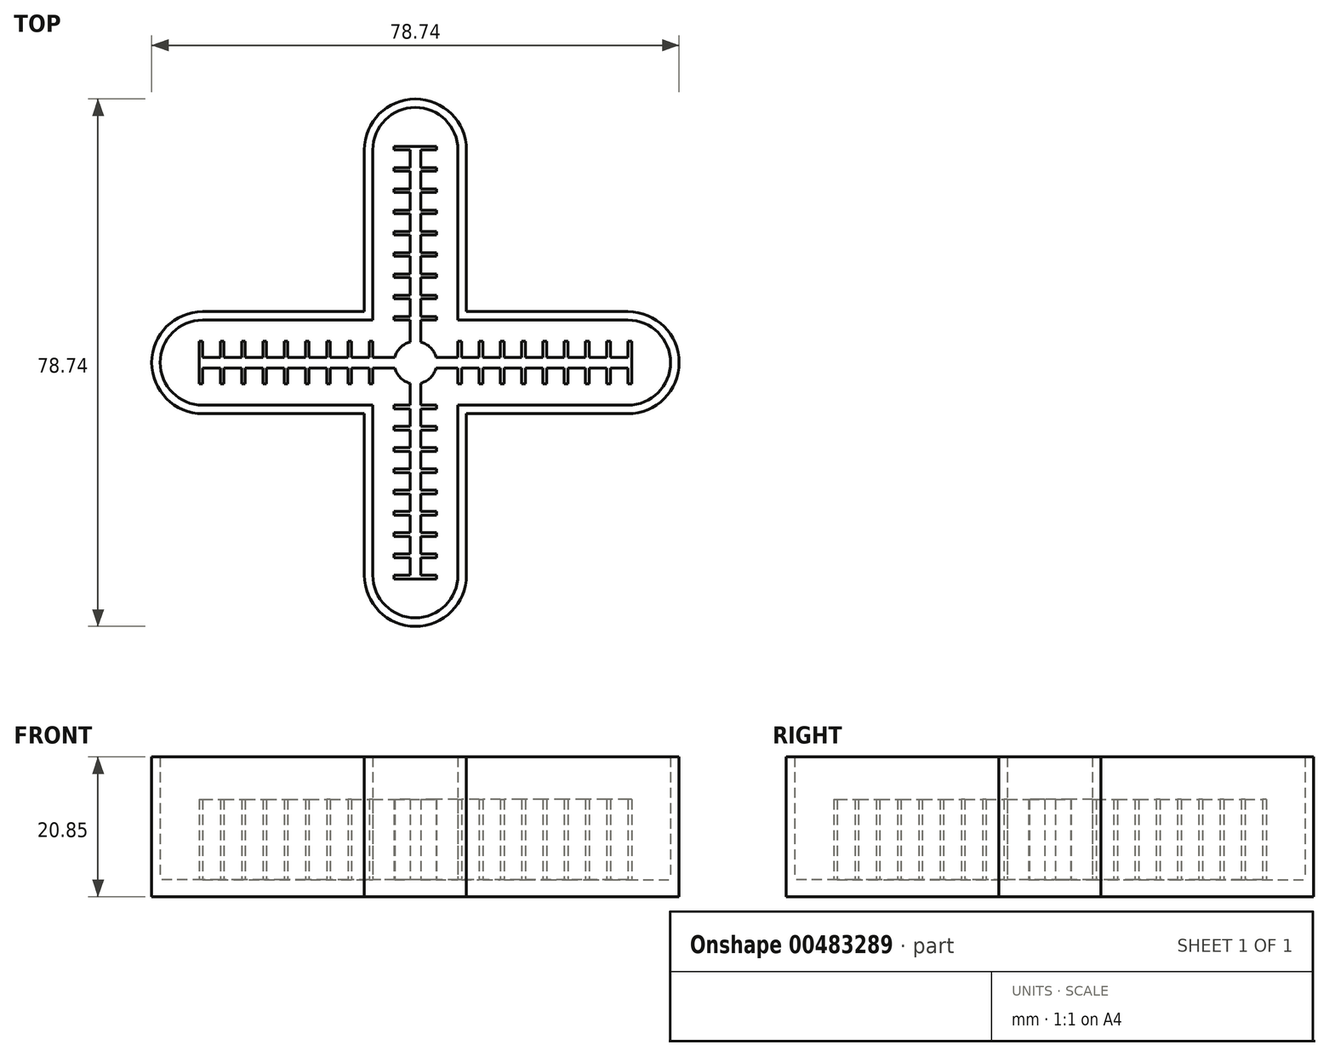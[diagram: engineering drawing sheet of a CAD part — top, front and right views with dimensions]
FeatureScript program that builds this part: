
annotation { "Feature Type Name" : "Feature", "Feature Type Description" : "" }
export const myFeature = defineFeature(function(context is Context, id is Id, definition is map)
    precondition{}
    {
        {
            var Q0;
            Q0=qCreatedBy(makeId("Top.planeOp"),FACE);
            var sketch = newSketch(context, id + "F0", { "sketchPlane" : qUnion([Q0])});
            skLineSegment(sketch, "E0", {"start": v(0, 0) * mm, "end": v(0, 25.4) * mm});
            skArc(sketch, "E1", {"start": v(6.35, 25.4) * mm, "mid": v(0, 31.75) * mm, "end": v(-6.35, 25.4) * mm});
            skLineSegment(sketch, "E2", {"start": v(6.35, 25.4) * mm, "end": v(6.35, 0) * mm});
            skLineSegment(sketch, "E3", {"start": v(-6.35, 25.4) * mm, "end": v(-6.35, 0) * mm});
            skLineSegment(sketch, "E4", {"start": v(6.35, 0) * mm, "end": v(31.75, 0) * mm});
            skLineSegment(sketch, "E5.0", {"start": v(6.35, -12.7) * mm, "end": v(31.75, -12.7) * mm});
            skArc(sketch, "E6", {"start": v(31.75, -12.7) * mm, "mid": v(38.1, -6.35) * mm, "end": v(31.75, 0) * mm});
            skLineSegment(sketch, "E7", {"start": v(31.75, -6.35) * mm, "end": v(6.35, -6.35) * mm});
            skLineSegment(sketch, "E8", {"start": v(6.35, -12.7) * mm, "end": v(6.35, -38.1) * mm});
            skLineSegment(sketch, "E9.0", {"start": v(-6.35, -12.7) * mm, "end": v(-6.35, -38.1) * mm});
            skArc(sketch, "E10", {"start": v(-6.35, -38.1) * mm, "mid": v(0, -44.45) * mm, "end": v(6.35, -38.1) * mm});
            skLineSegment(sketch, "E11", {"start": v(0, -38.1) * mm, "end": v(0, -12.7) * mm});
            skLineSegment(sketch, "E12", {"start": v(-6.35, -12.7) * mm, "end": v(-31.75, -12.7) * mm});
            skLineSegment(sketch, "E13.0", {"start": v(-6.35, 0) * mm, "end": v(-31.75, 0) * mm});
            skArc(sketch, "E14", {"start": v(-31.75, 0) * mm, "mid": v(-38.1, -6.35) * mm, "end": v(-31.75, -12.7) * mm});
            skLineSegment(sketch, "E15", {"start": v(-31.75, -6.35) * mm, "end": v(-6.35, -6.35) * mm});
            skLineSegment(sketch, "E16", {"start": v(-3.17, 0) * mm, "end": v(3.18, 0) * mm});
            skLineSegment(sketch, "E17.0", {"start": v(-3.17, 3.18) * mm, "end": v(3.18, 3.18) * mm});
            skLineSegment(sketch, "E18.0", {"start": v(-3.17, 6.35) * mm, "end": v(3.18, 6.35) * mm});
            skLineSegment(sketch, "E19.0", {"start": v(-3.17, 9.53) * mm, "end": v(3.18, 9.53) * mm});
            skLineSegment(sketch, "E20.0", {"start": v(-3.17, 12.7) * mm, "end": v(3.18, 12.7) * mm});
            skLineSegment(sketch, "E21.0", {"start": v(-3.17, 15.88) * mm, "end": v(3.18, 15.88) * mm});
            skLineSegment(sketch, "E22.0", {"start": v(-3.17, 19.05) * mm, "end": v(3.18, 19.05) * mm});
            skLineSegment(sketch, "E23.0", {"start": v(-3.17, 22.23) * mm, "end": v(3.18, 22.23) * mm});
            skLineSegment(sketch, "E24.0", {"start": v(-3.17, 25.4) * mm, "end": v(3.18, 25.4) * mm});
            skLineSegment(sketch, "E25.1.0", {"start": v(-31.75, -9.52) * mm, "end": v(-31.75, -3.17) * mm});
            skLineSegment(sketch, "E25.1.1", {"start": v(-28.58, -9.52) * mm, "end": v(-28.58, -3.17) * mm});
            skLineSegment(sketch, "E25.1.2", {"start": v(-25.4, -9.52) * mm, "end": v(-25.4, -3.17) * mm});
            skLineSegment(sketch, "E25.1.3", {"start": v(-22.23, -9.52) * mm, "end": v(-22.23, -3.17) * mm});
            skLineSegment(sketch, "E25.1.4", {"start": v(-19.05, -9.52) * mm, "end": v(-19.05, -3.17) * mm});
            skLineSegment(sketch, "E25.1.5", {"start": v(-15.88, -9.52) * mm, "end": v(-15.88, -3.17) * mm});
            skLineSegment(sketch, "E25.1.6", {"start": v(-12.7, -9.52) * mm, "end": v(-12.7, -3.17) * mm});
            skLineSegment(sketch, "E25.1.7", {"start": v(-9.53, -9.52) * mm, "end": v(-9.53, -3.17) * mm});
            skLineSegment(sketch, "E25.1.8", {"start": v(-6.35, -9.52) * mm, "end": v(-6.35, -3.17) * mm});
            skLineSegment(sketch, "E25.2.0", {"start": v(3.17, -38.1) * mm, "end": v(-3.18, -38.1) * mm});
            skLineSegment(sketch, "E25.2.1", {"start": v(3.17, -34.92) * mm, "end": v(-3.18, -34.92) * mm});
            skLineSegment(sketch, "E25.2.2", {"start": v(3.17, -31.75) * mm, "end": v(-3.18, -31.75) * mm});
            skLineSegment(sketch, "E25.2.3", {"start": v(3.17, -28.57) * mm, "end": v(-3.18, -28.57) * mm});
            skLineSegment(sketch, "E25.2.4", {"start": v(3.17, -25.4) * mm, "end": v(-3.18, -25.4) * mm});
            skLineSegment(sketch, "E25.2.5", {"start": v(3.17, -22.23) * mm, "end": v(-3.18, -22.23) * mm});
            skLineSegment(sketch, "E25.2.6", {"start": v(3.17, -19.05) * mm, "end": v(-3.18, -19.05) * mm});
            skLineSegment(sketch, "E25.2.7", {"start": v(3.17, -15.88) * mm, "end": v(-3.18, -15.88) * mm});
            skLineSegment(sketch, "E25.2.8", {"start": v(3.17, -12.7) * mm, "end": v(-3.18, -12.7) * mm});
            skLineSegment(sketch, "E25.3.0", {"start": v(31.75, -3.18) * mm, "end": v(31.75, -9.53) * mm});
            skLineSegment(sketch, "E25.3.1", {"start": v(28.58, -3.18) * mm, "end": v(28.58, -9.53) * mm});
            skLineSegment(sketch, "E25.3.2", {"start": v(25.4, -3.18) * mm, "end": v(25.4, -9.53) * mm});
            skLineSegment(sketch, "E25.3.3", {"start": v(22.23, -3.18) * mm, "end": v(22.23, -9.53) * mm});
            skLineSegment(sketch, "E25.3.4", {"start": v(19.05, -3.18) * mm, "end": v(19.05, -9.53) * mm});
            skLineSegment(sketch, "E25.3.5", {"start": v(15.88, -3.18) * mm, "end": v(15.88, -9.53) * mm});
            skLineSegment(sketch, "E25.3.6", {"start": v(12.7, -3.18) * mm, "end": v(12.7, -9.53) * mm});
            skLineSegment(sketch, "E25.3.7", {"start": v(9.53, -3.18) * mm, "end": v(9.53, -9.53) * mm});
            skLineSegment(sketch, "E25.3.8", {"start": v(6.35, -3.18) * mm, "end": v(6.35, -9.53) * mm});
            skPoint(sketch, "E25.center", {"position": v(0, -6.35) * mm});
            skCircle(sketch, "E26", {"center": v(0, -6.35) * mm, "radius": 3.18 * mm});
            skLineSegment(sketch, "E27", {"start": v(6.35, -6.35) * mm, "end": v(3.18, -6.35) * mm});
            skLineSegment(sketch, "E28", {"start": v(0, 0) * mm, "end": v(0, -3.17) * mm});
            skLineSegment(sketch, "E29", {"start": v(-6.35, -6.35) * mm, "end": v(-3.18, -6.35) * mm});
            skLineSegment(sketch, "E30", {"start": v(0, -12.7) * mm, "end": v(0, -9.53) * mm});
            skLineSegment(sketch, "E31.0", {"start": v(0.8, -38.1) * mm, "end": v(0.8, -12.7) * mm});
            skLineSegment(sketch, "E32.0", {"start": v(-0.8, -38.1) * mm, "end": v(-0.8, -12.7) * mm});
            skLineSegment(sketch, "E33", {"start": v(-0.8, -12.7) * mm, "end": v(-0.8, -9.42) * mm});
            skLineSegment(sketch, "E34", {"start": v(0.8, -12.7) * mm, "end": v(0.8, -9.42) * mm});
            skLineSegment(sketch, "E35.0", {"start": v(31.75, -5.56) * mm, "end": v(6.35, -5.56) * mm});
            skLineSegment(sketch, "E36.0", {"start": v(31.75, -7.14) * mm, "end": v(6.35, -7.14) * mm});
            skLineSegment(sketch, "E37", {"start": v(6.35, -7.14) * mm, "end": v(3.07, -7.14) * mm});
            skLineSegment(sketch, "E38", {"start": v(6.35, -5.56) * mm, "end": v(3.07, -5.56) * mm});
            skLineSegment(sketch, "E39.0", {"start": v(0.8, 0) * mm, "end": v(0.8, 25.4) * mm});
            skLineSegment(sketch, "E40.0", {"start": v(-0.8, 0) * mm, "end": v(-0.8, 25.4) * mm});
            skLineSegment(sketch, "E41", {"start": v(-0.8, 0) * mm, "end": v(-0.8, -3.28) * mm});
            skLineSegment(sketch, "E42", {"start": v(0.8, 0) * mm, "end": v(0.8, -3.28) * mm});
            skLineSegment(sketch, "E43.0", {"start": v(-31.75, -7.14) * mm, "end": v(-6.35, -7.14) * mm});
            skLineSegment(sketch, "E44.0", {"start": v(-31.75, -5.56) * mm, "end": v(-6.35, -5.56) * mm});
            skLineSegment(sketch, "E45", {"start": v(-6.35, -5.56) * mm, "end": v(-3.07, -5.56) * mm});
            skLineSegment(sketch, "E46", {"start": v(-6.35, -7.14) * mm, "end": v(-3.07, -7.14) * mm});
            skLineSegment(sketch, "E47.0", {"start": v(7.62, 25.4) * mm, "end": v(7.62, 1.27) * mm});
            skLineSegment(sketch, "E47.1", {"start": v(-7.62, -13.97) * mm, "end": v(-31.75, -13.97) * mm});
            skArc(sketch, "E47.2", {"start": v(-31.75, 1.27) * mm, "mid": v(-39.37, -6.35) * mm, "end": v(-31.75, -13.97) * mm});
            skLineSegment(sketch, "E47.3", {"start": v(-7.62, 1.27) * mm, "end": v(-31.75, 1.27) * mm});
            skLineSegment(sketch, "E47.4", {"start": v(-7.62, 25.4) * mm, "end": v(-7.62, 1.27) * mm});
            skLineSegment(sketch, "E47.5", {"start": v(-7.62, -13.97) * mm, "end": v(-7.62, -38.1) * mm});
            skArc(sketch, "E47.6", {"start": v(7.62, 25.4) * mm, "mid": v(0, 33.02) * mm, "end": v(-7.62, 25.4) * mm});
            skArc(sketch, "E47.7", {"start": v(-7.62, -38.1) * mm, "mid": v(0, -45.72) * mm, "end": v(7.62, -38.1) * mm});
            skLineSegment(sketch, "E47.8", {"start": v(7.62, -13.97) * mm, "end": v(7.62, -38.1) * mm});
            skLineSegment(sketch, "E47.9", {"start": v(7.62, -13.97) * mm, "end": v(31.75, -13.97) * mm});
            skArc(sketch, "E47.10", {"start": v(31.75, -13.97) * mm, "mid": v(39.37, -6.35) * mm, "end": v(31.75, 1.27) * mm});
            skLineSegment(sketch, "E47.11", {"start": v(7.62, 1.27) * mm, "end": v(31.75, 1.27) * mm});
            skLineSegment(sketch, "E48.0", {"start": v(6.88, -3.18) * mm, "end": v(6.88, -9.53) * mm});
            skLineSegment(sketch, "E49", {"start": v(6.35, -3.18) * mm, "end": v(6.88, -3.18) * mm});
            skLineSegment(sketch, "E50", {"start": v(6.35, -9.53) * mm, "end": v(6.88, -9.53) * mm});
            skLineSegment(sketch, "E51.0", {"start": v(10.05, -3.18) * mm, "end": v(10.05, -9.53) * mm});
            skLineSegment(sketch, "E52", {"start": v(9.53, -3.18) * mm, "end": v(10.05, -3.18) * mm});
            skLineSegment(sketch, "E53", {"start": v(9.53, -9.53) * mm, "end": v(10.05, -9.53) * mm});
            skLineSegment(sketch, "E54.0", {"start": v(13.23, -3.18) * mm, "end": v(13.23, -9.53) * mm});
            skLineSegment(sketch, "E55", {"start": v(12.7, -3.18) * mm, "end": v(13.23, -3.18) * mm});
            skLineSegment(sketch, "E56", {"start": v(12.7, -9.53) * mm, "end": v(13.23, -9.53) * mm});
            skLineSegment(sketch, "E57.0", {"start": v(16.4, -3.18) * mm, "end": v(16.4, -9.53) * mm});
            skLineSegment(sketch, "E58", {"start": v(16.4, -3.18) * mm, "end": v(15.88, -3.18) * mm});
            skLineSegment(sketch, "E59", {"start": v(16.4, -9.53) * mm, "end": v(15.88, -9.53) * mm});
            skLineSegment(sketch, "E60.0", {"start": v(19.58, -3.18) * mm, "end": v(19.58, -9.53) * mm});
            skLineSegment(sketch, "E61", {"start": v(19.58, -3.18) * mm, "end": v(19.05, -3.18) * mm});
            skLineSegment(sketch, "E62", {"start": v(19.58, -9.53) * mm, "end": v(19.05, -9.53) * mm});
            skLineSegment(sketch, "E63.0", {"start": v(22.75, -3.18) * mm, "end": v(22.75, -9.53) * mm});
            skLineSegment(sketch, "E64", {"start": v(22.75, -3.18) * mm, "end": v(22.23, -3.18) * mm});
            skLineSegment(sketch, "E65", {"start": v(22.75, -9.53) * mm, "end": v(22.23, -9.53) * mm});
            skLineSegment(sketch, "E66.0", {"start": v(25.93, -3.18) * mm, "end": v(25.93, -9.53) * mm});
            skLineSegment(sketch, "E67", {"start": v(25.93, -3.18) * mm, "end": v(25.4, -3.18) * mm});
            skLineSegment(sketch, "E68", {"start": v(25.93, -9.53) * mm, "end": v(25.4, -9.53) * mm});
            skLineSegment(sketch, "E69.0", {"start": v(29.1, -3.18) * mm, "end": v(29.1, -9.53) * mm});
            skLineSegment(sketch, "E70", {"start": v(29.1, -3.18) * mm, "end": v(28.58, -3.18) * mm});
            skLineSegment(sketch, "E71", {"start": v(29.1, -9.53) * mm, "end": v(28.58, -9.53) * mm});
            skLineSegment(sketch, "E72.0", {"start": v(32.28, -3.18) * mm, "end": v(32.28, -9.53) * mm});
            skLineSegment(sketch, "E73", {"start": v(32.28, -3.18) * mm, "end": v(31.75, -3.18) * mm});
            skLineSegment(sketch, "E74", {"start": v(32.28, -9.53) * mm, "end": v(31.75, -9.53) * mm});
            skLineSegment(sketch, "E75.1.0", {"start": v(-3.17, 25.93) * mm, "end": v(3.18, 25.93) * mm});
            skLineSegment(sketch, "E75.1.1", {"start": v(-3.17, 25.93) * mm, "end": v(-3.17, 25.4) * mm});
            skLineSegment(sketch, "E75.1.2", {"start": v(3.18, 25.93) * mm, "end": v(3.18, 25.4) * mm});
            skLineSegment(sketch, "E75.1.3", {"start": v(-3.17, 22.75) * mm, "end": v(3.18, 22.75) * mm});
            skLineSegment(sketch, "E75.1.4", {"start": v(3.18, 22.75) * mm, "end": v(3.18, 22.23) * mm});
            skLineSegment(sketch, "E75.1.5", {"start": v(-3.17, 22.75) * mm, "end": v(-3.17, 22.23) * mm});
            skLineSegment(sketch, "E75.1.6", {"start": v(-3.17, 19.58) * mm, "end": v(3.18, 19.58) * mm});
            skLineSegment(sketch, "E75.1.7", {"start": v(-3.17, 19.58) * mm, "end": v(-3.17, 19.05) * mm});
            skLineSegment(sketch, "E75.1.8", {"start": v(3.18, 19.58) * mm, "end": v(3.18, 19.05) * mm});
            skLineSegment(sketch, "E75.1.9", {"start": v(-3.17, 16.4) * mm, "end": v(3.18, 16.4) * mm});
            skLineSegment(sketch, "E75.1.10", {"start": v(-3.17, 16.4) * mm, "end": v(-3.17, 15.88) * mm});
            skLineSegment(sketch, "E75.1.11", {"start": v(3.18, 16.4) * mm, "end": v(3.18, 15.88) * mm});
            skLineSegment(sketch, "E75.1.12", {"start": v(-3.17, 13.23) * mm, "end": v(3.18, 13.23) * mm});
            skLineSegment(sketch, "E75.1.13", {"start": v(3.18, 13.23) * mm, "end": v(3.18, 12.7) * mm});
            skLineSegment(sketch, "E75.1.14", {"start": v(-3.17, 13.23) * mm, "end": v(-3.17, 12.7) * mm});
            skLineSegment(sketch, "E75.1.15", {"start": v(-3.17, 10.05) * mm, "end": v(3.18, 10.05) * mm});
            skLineSegment(sketch, "E75.1.16", {"start": v(-3.17, 10.05) * mm, "end": v(-3.17, 9.53) * mm});
            skLineSegment(sketch, "E75.1.17", {"start": v(3.18, 10.05) * mm, "end": v(3.18, 9.53) * mm});
            skLineSegment(sketch, "E75.1.18", {"start": v(-3.17, 6.88) * mm, "end": v(3.18, 6.88) * mm});
            skLineSegment(sketch, "E75.1.19", {"start": v(3.18, 6.35) * mm, "end": v(3.18, 6.88) * mm});
            skLineSegment(sketch, "E75.1.20", {"start": v(-3.17, 6.35) * mm, "end": v(-3.17, 6.88) * mm});
            skLineSegment(sketch, "E75.1.21", {"start": v(-3.17, 3.7) * mm, "end": v(3.18, 3.7) * mm});
            skLineSegment(sketch, "E75.1.22", {"start": v(3.18, 3.18) * mm, "end": v(3.18, 3.7) * mm});
            skLineSegment(sketch, "E75.1.23", {"start": v(-3.17, 3.18) * mm, "end": v(-3.17, 3.7) * mm});
            skLineSegment(sketch, "E75.1.24", {"start": v(3.18, 0) * mm, "end": v(3.18, 0.53) * mm});
            skLineSegment(sketch, "E75.1.25", {"start": v(-3.17, 0.53) * mm, "end": v(3.18, 0.53) * mm});
            skLineSegment(sketch, "E75.1.26", {"start": v(-3.17, 0) * mm, "end": v(-3.17, 0.53) * mm});
            skLineSegment(sketch, "E75.2.0", {"start": v(-32.28, -9.52) * mm, "end": v(-32.28, -3.17) * mm});
            skLineSegment(sketch, "E75.2.1", {"start": v(-32.28, -9.52) * mm, "end": v(-31.75, -9.52) * mm});
            skLineSegment(sketch, "E75.2.2", {"start": v(-32.28, -3.17) * mm, "end": v(-31.75, -3.17) * mm});
            skLineSegment(sketch, "E75.2.3", {"start": v(-29.1, -9.52) * mm, "end": v(-29.1, -3.17) * mm});
            skLineSegment(sketch, "E75.2.4", {"start": v(-29.1, -3.17) * mm, "end": v(-28.58, -3.17) * mm});
            skLineSegment(sketch, "E75.2.5", {"start": v(-29.1, -9.52) * mm, "end": v(-28.58, -9.52) * mm});
            skLineSegment(sketch, "E75.2.6", {"start": v(-25.93, -9.52) * mm, "end": v(-25.93, -3.17) * mm});
            skLineSegment(sketch, "E75.2.7", {"start": v(-25.93, -9.52) * mm, "end": v(-25.4, -9.52) * mm});
            skLineSegment(sketch, "E75.2.8", {"start": v(-25.93, -3.17) * mm, "end": v(-25.4, -3.17) * mm});
            skLineSegment(sketch, "E75.2.9", {"start": v(-22.75, -9.52) * mm, "end": v(-22.75, -3.17) * mm});
            skLineSegment(sketch, "E75.2.10", {"start": v(-22.75, -9.52) * mm, "end": v(-22.23, -9.52) * mm});
            skLineSegment(sketch, "E75.2.11", {"start": v(-22.75, -3.17) * mm, "end": v(-22.23, -3.17) * mm});
            skLineSegment(sketch, "E75.2.12", {"start": v(-19.58, -9.52) * mm, "end": v(-19.58, -3.17) * mm});
            skLineSegment(sketch, "E75.2.13", {"start": v(-19.58, -3.17) * mm, "end": v(-19.05, -3.17) * mm});
            skLineSegment(sketch, "E75.2.14", {"start": v(-19.58, -9.52) * mm, "end": v(-19.05, -9.52) * mm});
            skLineSegment(sketch, "E75.2.15", {"start": v(-16.4, -9.52) * mm, "end": v(-16.4, -3.17) * mm});
            skLineSegment(sketch, "E75.2.16", {"start": v(-16.4, -9.52) * mm, "end": v(-15.88, -9.52) * mm});
            skLineSegment(sketch, "E75.2.17", {"start": v(-16.4, -3.17) * mm, "end": v(-15.88, -3.17) * mm});
            skLineSegment(sketch, "E75.2.18", {"start": v(-13.23, -9.52) * mm, "end": v(-13.23, -3.17) * mm});
            skLineSegment(sketch, "E75.2.19", {"start": v(-12.7, -3.17) * mm, "end": v(-13.23, -3.17) * mm});
            skLineSegment(sketch, "E75.2.20", {"start": v(-12.7, -9.52) * mm, "end": v(-13.23, -9.52) * mm});
            skLineSegment(sketch, "E75.2.21", {"start": v(-10.05, -9.52) * mm, "end": v(-10.05, -3.17) * mm});
            skLineSegment(sketch, "E75.2.22", {"start": v(-9.52, -3.17) * mm, "end": v(-10.05, -3.17) * mm});
            skLineSegment(sketch, "E75.2.23", {"start": v(-9.53, -9.52) * mm, "end": v(-10.05, -9.52) * mm});
            skLineSegment(sketch, "E75.2.24", {"start": v(-6.35, -3.17) * mm, "end": v(-6.88, -3.17) * mm});
            skLineSegment(sketch, "E75.2.25", {"start": v(-6.88, -9.52) * mm, "end": v(-6.88, -3.17) * mm});
            skLineSegment(sketch, "E75.2.26", {"start": v(-6.35, -9.52) * mm, "end": v(-6.88, -9.52) * mm});
            skLineSegment(sketch, "E75.3.0", {"start": v(3.17, -38.63) * mm, "end": v(-3.18, -38.63) * mm});
            skLineSegment(sketch, "E75.3.1", {"start": v(3.17, -38.63) * mm, "end": v(3.17, -38.1) * mm});
            skLineSegment(sketch, "E75.3.2", {"start": v(-3.18, -38.63) * mm, "end": v(-3.18, -38.1) * mm});
            skLineSegment(sketch, "E75.3.3", {"start": v(3.17, -35.45) * mm, "end": v(-3.18, -35.45) * mm});
            skLineSegment(sketch, "E75.3.4", {"start": v(-3.18, -35.45) * mm, "end": v(-3.18, -34.92) * mm});
            skLineSegment(sketch, "E75.3.5", {"start": v(3.17, -35.45) * mm, "end": v(3.17, -34.93) * mm});
            skLineSegment(sketch, "E75.3.6", {"start": v(3.17, -32.28) * mm, "end": v(-3.18, -32.28) * mm});
            skLineSegment(sketch, "E75.3.7", {"start": v(3.17, -32.28) * mm, "end": v(3.17, -31.75) * mm});
            skLineSegment(sketch, "E75.3.8", {"start": v(-3.18, -32.28) * mm, "end": v(-3.18, -31.75) * mm});
            skLineSegment(sketch, "E75.3.9", {"start": v(3.17, -29.1) * mm, "end": v(-3.18, -29.1) * mm});
            skLineSegment(sketch, "E75.3.10", {"start": v(3.17, -29.1) * mm, "end": v(3.17, -28.58) * mm});
            skLineSegment(sketch, "E75.3.11", {"start": v(-3.18, -29.1) * mm, "end": v(-3.18, -28.57) * mm});
            skLineSegment(sketch, "E75.3.12", {"start": v(3.17, -25.93) * mm, "end": v(-3.18, -25.93) * mm});
            skLineSegment(sketch, "E75.3.13", {"start": v(-3.18, -25.93) * mm, "end": v(-3.18, -25.4) * mm});
            skLineSegment(sketch, "E75.3.14", {"start": v(3.17, -25.93) * mm, "end": v(3.17, -25.4) * mm});
            skLineSegment(sketch, "E75.3.15", {"start": v(3.17, -22.75) * mm, "end": v(-3.18, -22.75) * mm});
            skLineSegment(sketch, "E75.3.16", {"start": v(3.17, -22.75) * mm, "end": v(3.17, -22.23) * mm});
            skLineSegment(sketch, "E75.3.17", {"start": v(-3.18, -22.75) * mm, "end": v(-3.18, -22.22) * mm});
            skLineSegment(sketch, "E75.3.18", {"start": v(3.17, -19.58) * mm, "end": v(-3.18, -19.58) * mm});
            skLineSegment(sketch, "E75.3.19", {"start": v(-3.18, -19.05) * mm, "end": v(-3.18, -19.58) * mm});
            skLineSegment(sketch, "E75.3.20", {"start": v(3.17, -19.05) * mm, "end": v(3.17, -19.58) * mm});
            skLineSegment(sketch, "E75.3.21", {"start": v(3.17, -16.4) * mm, "end": v(-3.18, -16.4) * mm});
            skLineSegment(sketch, "E75.3.22", {"start": v(-3.18, -15.88) * mm, "end": v(-3.18, -16.4) * mm});
            skLineSegment(sketch, "E75.3.23", {"start": v(3.17, -15.88) * mm, "end": v(3.17, -16.4) * mm});
            skLineSegment(sketch, "E75.3.24", {"start": v(-3.18, -12.7) * mm, "end": v(-3.18, -13.23) * mm});
            skLineSegment(sketch, "E75.3.25", {"start": v(3.17, -13.23) * mm, "end": v(-3.18, -13.23) * mm});
            skLineSegment(sketch, "E75.3.26", {"start": v(3.17, -12.7) * mm, "end": v(3.17, -13.23) * mm});
            skSolve(sketch);
        }
        {
            var Q0;
            Q0=makeQuery(id+"F0.imprint","IMPRINT",FACE,{"disambiguationData":[TD([[makeQuery(id+"F0.imprint","IMPRINT",EDGE,{"derivedFrom":sQuery(id+"F0.wireOp",EDGE,"E1")}),-1.0]])]});
            extrude(context, id + "F1", {"entities" : qUnion([Q0]), "depth" : 19.05 * mm});
        }
        {
            var Q0;
            Q0=makeQuery(id+"F0.imprint","IMPRINT",FACE,{"disambiguationData":[TD([[makeQuery(id+"F0.imprint","IMPRINT",EDGE,{"derivedFrom":sQuery(id+"F0.wireOp",EDGE,"E75.2.0")}),-1.0]])]});
            var Q1;
            {var subQ0=sQuery(id+"F0.wireOp",EDGE,"E25.1.0");var subQ1=sQuery(id+"F0.wireOp",EDGE,"E15");var subQ2=makeQuery(id+"F0.imprint","INTERSECT",VERTEX,{"derivedFrom":[subQ1,subQ0]});Q1=makeQuery(id+"F0.imprint","IMPRINT",FACE,{"disambiguationData":[TD([[makeQuery(id+"F0.imprint","IMPRINT",EDGE,{"disambiguationData":[TD([[subQ2,-1.0]])],"derivedFrom":subQ1}),1.0]])]});}
            var Q2;
            {var subQ0=sQuery(id+"F0.wireOp",EDGE,"E25.1.0");var subQ1=sQuery(id+"F0.wireOp",EDGE,"E15");var subQ2=makeQuery(id+"F0.imprint","INTERSECT",VERTEX,{"derivedFrom":[subQ1,subQ0]});Q2=makeQuery(id+"F0.imprint","IMPRINT",FACE,{"disambiguationData":[TD([[makeQuery(id+"F0.imprint","IMPRINT",EDGE,{"disambiguationData":[TD([[subQ2,-1.0]])],"derivedFrom":subQ1}),-1.0]])]});}
            var Q3;
            {var subQ0=sQuery(id+"F0.wireOp",EDGE,"E75.2.3");var subQ1=sQuery(id+"F0.wireOp",EDGE,"E15");var subQ2=makeQuery(id+"F0.imprint","INTERSECT",VERTEX,{"derivedFrom":[subQ1,subQ0]});Q3=makeQuery(id+"F0.imprint","IMPRINT",FACE,{"disambiguationData":[TD([[makeQuery(id+"F0.imprint","IMPRINT",EDGE,{"disambiguationData":[TD([[subQ2,-1.0]])],"derivedFrom":subQ1}),-1.0]])]});}
            var Q4;
            {var subQ0=sQuery(id+"F0.wireOp",EDGE,"E75.2.3");var subQ1=sQuery(id+"F0.wireOp",EDGE,"E15");var subQ2=makeQuery(id+"F0.imprint","INTERSECT",VERTEX,{"derivedFrom":[subQ1,subQ0]});Q4=makeQuery(id+"F0.imprint","IMPRINT",FACE,{"disambiguationData":[TD([[makeQuery(id+"F0.imprint","IMPRINT",EDGE,{"disambiguationData":[TD([[subQ2,-1.0]])],"derivedFrom":subQ1}),1.0]])]});}
            var Q5;
            {var subQ0=sQuery(id+"F0.wireOp",EDGE,"E75.2.4");Q5=makeQuery(id+"F0.imprint","IMPRINT",FACE,{"disambiguationData":[TD([[makeQuery(id+"F0.imprint","IMPRINT",EDGE,{"derivedFrom":subQ0}),-1.0]])]});}
            var Q6;
            {var subQ0=sQuery(id+"F0.wireOp",EDGE,"E25.1.1");var subQ1=sQuery(id+"F0.wireOp",EDGE,"E15");var subQ2=makeQuery(id+"F0.imprint","INTERSECT",VERTEX,{"derivedFrom":[subQ1,subQ0]});Q6=makeQuery(id+"F0.imprint","IMPRINT",FACE,{"disambiguationData":[TD([[makeQuery(id+"F0.imprint","IMPRINT",EDGE,{"disambiguationData":[TD([[subQ2,-1.0]])],"derivedFrom":subQ1}),1.0]])]});}
            var Q7;
            {var subQ0=sQuery(id+"F0.wireOp",EDGE,"E25.1.1");var subQ1=sQuery(id+"F0.wireOp",EDGE,"E15");var subQ2=makeQuery(id+"F0.imprint","INTERSECT",VERTEX,{"derivedFrom":[subQ1,subQ0]});Q7=makeQuery(id+"F0.imprint","IMPRINT",FACE,{"disambiguationData":[TD([[makeQuery(id+"F0.imprint","IMPRINT",EDGE,{"disambiguationData":[TD([[subQ2,-1.0]])],"derivedFrom":subQ1}),-1.0]])]});}
            var Q8;
            {var subQ0=sQuery(id+"F0.wireOp",EDGE,"E75.2.5");Q8=makeQuery(id+"F0.imprint","IMPRINT",FACE,{"disambiguationData":[TD([[makeQuery(id+"F0.imprint","IMPRINT",EDGE,{"derivedFrom":subQ0}),1.0]])]});}
            var Q9;
            {var subQ0=sQuery(id+"F0.wireOp",EDGE,"E75.2.6");var subQ1=sQuery(id+"F0.wireOp",EDGE,"E15");var subQ2=makeQuery(id+"F0.imprint","INTERSECT",VERTEX,{"derivedFrom":[subQ1,subQ0]});Q9=makeQuery(id+"F0.imprint","IMPRINT",FACE,{"disambiguationData":[TD([[makeQuery(id+"F0.imprint","IMPRINT",EDGE,{"disambiguationData":[TD([[subQ2,-1.0]])],"derivedFrom":subQ1}),-1.0]])]});}
            var Q10;
            {var subQ0=sQuery(id+"F0.wireOp",EDGE,"E75.2.6");var subQ1=sQuery(id+"F0.wireOp",EDGE,"E15");var subQ2=makeQuery(id+"F0.imprint","INTERSECT",VERTEX,{"derivedFrom":[subQ1,subQ0]});Q10=makeQuery(id+"F0.imprint","IMPRINT",FACE,{"disambiguationData":[TD([[makeQuery(id+"F0.imprint","IMPRINT",EDGE,{"disambiguationData":[TD([[subQ2,-1.0]])],"derivedFrom":subQ1}),1.0]])]});}
            var Q11;
            {var subQ0=sQuery(id+"F0.wireOp",EDGE,"E75.2.8");Q11=makeQuery(id+"F0.imprint","IMPRINT",FACE,{"disambiguationData":[TD([[makeQuery(id+"F0.imprint","IMPRINT",EDGE,{"derivedFrom":subQ0}),-1.0]])]});}
            var Q12;
            {var subQ0=sQuery(id+"F0.wireOp",EDGE,"E75.2.7");Q12=makeQuery(id+"F0.imprint","IMPRINT",FACE,{"disambiguationData":[TD([[makeQuery(id+"F0.imprint","IMPRINT",EDGE,{"derivedFrom":subQ0}),1.0]])]});}
            var Q13;
            {var subQ0=sQuery(id+"F0.wireOp",EDGE,"E25.1.2");var subQ1=sQuery(id+"F0.wireOp",EDGE,"E15");var subQ2=makeQuery(id+"F0.imprint","INTERSECT",VERTEX,{"derivedFrom":[subQ1,subQ0]});Q13=makeQuery(id+"F0.imprint","IMPRINT",FACE,{"disambiguationData":[TD([[makeQuery(id+"F0.imprint","IMPRINT",EDGE,{"disambiguationData":[TD([[subQ2,-1.0]])],"derivedFrom":subQ1}),-1.0]])]});}
            var Q14;
            {var subQ0=sQuery(id+"F0.wireOp",EDGE,"E25.1.2");var subQ1=sQuery(id+"F0.wireOp",EDGE,"E15");var subQ2=makeQuery(id+"F0.imprint","INTERSECT",VERTEX,{"derivedFrom":[subQ1,subQ0]});Q14=makeQuery(id+"F0.imprint","IMPRINT",FACE,{"disambiguationData":[TD([[makeQuery(id+"F0.imprint","IMPRINT",EDGE,{"disambiguationData":[TD([[subQ2,-1.0]])],"derivedFrom":subQ1}),1.0]])]});}
            var Q15;
            {var subQ0=sQuery(id+"F0.wireOp",EDGE,"E75.2.10");Q15=makeQuery(id+"F0.imprint","IMPRINT",FACE,{"disambiguationData":[TD([[makeQuery(id+"F0.imprint","IMPRINT",EDGE,{"derivedFrom":subQ0}),1.0]])]});}
            var Q16;
            {var subQ0=sQuery(id+"F0.wireOp",EDGE,"E75.2.9");var subQ1=sQuery(id+"F0.wireOp",EDGE,"E15");var subQ2=makeQuery(id+"F0.imprint","INTERSECT",VERTEX,{"derivedFrom":[subQ1,subQ0]});Q16=makeQuery(id+"F0.imprint","IMPRINT",FACE,{"disambiguationData":[TD([[makeQuery(id+"F0.imprint","IMPRINT",EDGE,{"disambiguationData":[TD([[subQ2,-1.0]])],"derivedFrom":subQ1}),-1.0]])]});}
            var Q17;
            {var subQ0=sQuery(id+"F0.wireOp",EDGE,"E75.2.9");var subQ1=sQuery(id+"F0.wireOp",EDGE,"E15");var subQ2=makeQuery(id+"F0.imprint","INTERSECT",VERTEX,{"derivedFrom":[subQ1,subQ0]});Q17=makeQuery(id+"F0.imprint","IMPRINT",FACE,{"disambiguationData":[TD([[makeQuery(id+"F0.imprint","IMPRINT",EDGE,{"disambiguationData":[TD([[subQ2,-1.0]])],"derivedFrom":subQ1}),1.0]])]});}
            var Q18;
            {var subQ0=sQuery(id+"F0.wireOp",EDGE,"E25.1.3");var subQ1=sQuery(id+"F0.wireOp",EDGE,"E15");var subQ2=makeQuery(id+"F0.imprint","INTERSECT",VERTEX,{"derivedFrom":[subQ1,subQ0]});Q18=makeQuery(id+"F0.imprint","IMPRINT",FACE,{"disambiguationData":[TD([[makeQuery(id+"F0.imprint","IMPRINT",EDGE,{"disambiguationData":[TD([[subQ2,-1.0]])],"derivedFrom":subQ1}),-1.0]])]});}
            var Q19;
            {var subQ0=sQuery(id+"F0.wireOp",EDGE,"E75.2.11");Q19=makeQuery(id+"F0.imprint","IMPRINT",FACE,{"disambiguationData":[TD([[makeQuery(id+"F0.imprint","IMPRINT",EDGE,{"derivedFrom":subQ0}),-1.0]])]});}
            var Q20;
            {var subQ0=sQuery(id+"F0.wireOp",EDGE,"E25.1.3");var subQ1=sQuery(id+"F0.wireOp",EDGE,"E15");var subQ2=makeQuery(id+"F0.imprint","INTERSECT",VERTEX,{"derivedFrom":[subQ1,subQ0]});Q20=makeQuery(id+"F0.imprint","IMPRINT",FACE,{"disambiguationData":[TD([[makeQuery(id+"F0.imprint","IMPRINT",EDGE,{"disambiguationData":[TD([[subQ2,-1.0]])],"derivedFrom":subQ1}),1.0]])]});}
            var Q21;
            {var subQ0=sQuery(id+"F0.wireOp",EDGE,"E75.2.12");var subQ1=sQuery(id+"F0.wireOp",EDGE,"E15");var subQ2=makeQuery(id+"F0.imprint","INTERSECT",VERTEX,{"derivedFrom":[subQ1,subQ0]});Q21=makeQuery(id+"F0.imprint","IMPRINT",FACE,{"disambiguationData":[TD([[makeQuery(id+"F0.imprint","IMPRINT",EDGE,{"disambiguationData":[TD([[subQ2,-1.0]])],"derivedFrom":subQ1}),-1.0]])]});}
            var Q22;
            {var subQ0=sQuery(id+"F0.wireOp",EDGE,"E75.2.12");var subQ1=sQuery(id+"F0.wireOp",EDGE,"E15");var subQ2=makeQuery(id+"F0.imprint","INTERSECT",VERTEX,{"derivedFrom":[subQ1,subQ0]});Q22=makeQuery(id+"F0.imprint","IMPRINT",FACE,{"disambiguationData":[TD([[makeQuery(id+"F0.imprint","IMPRINT",EDGE,{"disambiguationData":[TD([[subQ2,-1.0]])],"derivedFrom":subQ1}),1.0]])]});}
            var Q23;
            {var subQ0=sQuery(id+"F0.wireOp",EDGE,"E75.2.13");Q23=makeQuery(id+"F0.imprint","IMPRINT",FACE,{"disambiguationData":[TD([[makeQuery(id+"F0.imprint","IMPRINT",EDGE,{"derivedFrom":subQ0}),-1.0]])]});}
            var Q24;
            {var subQ0=sQuery(id+"F0.wireOp",EDGE,"E75.2.14");Q24=makeQuery(id+"F0.imprint","IMPRINT",FACE,{"disambiguationData":[TD([[makeQuery(id+"F0.imprint","IMPRINT",EDGE,{"derivedFrom":subQ0}),1.0]])]});}
            var Q25;
            {var subQ0=sQuery(id+"F0.wireOp",EDGE,"E25.1.4");var subQ1=sQuery(id+"F0.wireOp",EDGE,"E15");var subQ2=makeQuery(id+"F0.imprint","INTERSECT",VERTEX,{"derivedFrom":[subQ1,subQ0]});Q25=makeQuery(id+"F0.imprint","IMPRINT",FACE,{"disambiguationData":[TD([[makeQuery(id+"F0.imprint","IMPRINT",EDGE,{"disambiguationData":[TD([[subQ2,-1.0]])],"derivedFrom":subQ1}),-1.0]])]});}
            var Q26;
            {var subQ0=sQuery(id+"F0.wireOp",EDGE,"E25.1.4");var subQ1=sQuery(id+"F0.wireOp",EDGE,"E15");var subQ2=makeQuery(id+"F0.imprint","INTERSECT",VERTEX,{"derivedFrom":[subQ1,subQ0]});Q26=makeQuery(id+"F0.imprint","IMPRINT",FACE,{"disambiguationData":[TD([[makeQuery(id+"F0.imprint","IMPRINT",EDGE,{"disambiguationData":[TD([[subQ2,-1.0]])],"derivedFrom":subQ1}),1.0]])]});}
            var Q27;
            {var subQ0=sQuery(id+"F0.wireOp",EDGE,"E75.2.17");Q27=makeQuery(id+"F0.imprint","IMPRINT",FACE,{"disambiguationData":[TD([[makeQuery(id+"F0.imprint","IMPRINT",EDGE,{"derivedFrom":subQ0}),-1.0]])]});}
            var Q28;
            {var subQ0=sQuery(id+"F0.wireOp",EDGE,"E75.2.15");var subQ1=sQuery(id+"F0.wireOp",EDGE,"E15");var subQ2=makeQuery(id+"F0.imprint","INTERSECT",VERTEX,{"derivedFrom":[subQ1,subQ0]});Q28=makeQuery(id+"F0.imprint","IMPRINT",FACE,{"disambiguationData":[TD([[makeQuery(id+"F0.imprint","IMPRINT",EDGE,{"disambiguationData":[TD([[subQ2,-1.0]])],"derivedFrom":subQ1}),1.0]])]});}
            var Q29;
            {var subQ0=sQuery(id+"F0.wireOp",EDGE,"E75.2.15");var subQ1=sQuery(id+"F0.wireOp",EDGE,"E15");var subQ2=makeQuery(id+"F0.imprint","INTERSECT",VERTEX,{"derivedFrom":[subQ1,subQ0]});Q29=makeQuery(id+"F0.imprint","IMPRINT",FACE,{"disambiguationData":[TD([[makeQuery(id+"F0.imprint","IMPRINT",EDGE,{"disambiguationData":[TD([[subQ2,-1.0]])],"derivedFrom":subQ1}),-1.0]])]});}
            var Q30;
            {var subQ0=sQuery(id+"F0.wireOp",EDGE,"E75.2.16");Q30=makeQuery(id+"F0.imprint","IMPRINT",FACE,{"disambiguationData":[TD([[makeQuery(id+"F0.imprint","IMPRINT",EDGE,{"derivedFrom":subQ0}),1.0]])]});}
            var Q31;
            {var subQ0=sQuery(id+"F0.wireOp",EDGE,"E25.1.5");var subQ1=sQuery(id+"F0.wireOp",EDGE,"E15");var subQ2=makeQuery(id+"F0.imprint","INTERSECT",VERTEX,{"derivedFrom":[subQ1,subQ0]});Q31=makeQuery(id+"F0.imprint","IMPRINT",FACE,{"disambiguationData":[TD([[makeQuery(id+"F0.imprint","IMPRINT",EDGE,{"disambiguationData":[TD([[subQ2,-1.0]])],"derivedFrom":subQ1}),-1.0]])]});}
            var Q32;
            {var subQ0=sQuery(id+"F0.wireOp",EDGE,"E25.1.5");var subQ1=sQuery(id+"F0.wireOp",EDGE,"E15");var subQ2=makeQuery(id+"F0.imprint","INTERSECT",VERTEX,{"derivedFrom":[subQ1,subQ0]});Q32=makeQuery(id+"F0.imprint","IMPRINT",FACE,{"disambiguationData":[TD([[makeQuery(id+"F0.imprint","IMPRINT",EDGE,{"disambiguationData":[TD([[subQ2,-1.0]])],"derivedFrom":subQ1}),1.0]])]});}
            var Q33;
            {var subQ0=sQuery(id+"F0.wireOp",EDGE,"E75.2.19");Q33=makeQuery(id+"F0.imprint","IMPRINT",FACE,{"disambiguationData":[TD([[makeQuery(id+"F0.imprint","IMPRINT",EDGE,{"derivedFrom":subQ0}),1.0]])]});}
            var Q34;
            {var subQ0=sQuery(id+"F0.wireOp",EDGE,"E75.2.18");var subQ1=sQuery(id+"F0.wireOp",EDGE,"E15");var subQ2=makeQuery(id+"F0.imprint","INTERSECT",VERTEX,{"derivedFrom":[subQ1,subQ0]});Q34=makeQuery(id+"F0.imprint","IMPRINT",FACE,{"disambiguationData":[TD([[makeQuery(id+"F0.imprint","IMPRINT",EDGE,{"disambiguationData":[TD([[subQ2,-1.0]])],"derivedFrom":subQ1}),1.0]])]});}
            var Q35;
            {var subQ0=sQuery(id+"F0.wireOp",EDGE,"E75.2.18");var subQ1=sQuery(id+"F0.wireOp",EDGE,"E15");var subQ2=makeQuery(id+"F0.imprint","INTERSECT",VERTEX,{"derivedFrom":[subQ1,subQ0]});Q35=makeQuery(id+"F0.imprint","IMPRINT",FACE,{"disambiguationData":[TD([[makeQuery(id+"F0.imprint","IMPRINT",EDGE,{"disambiguationData":[TD([[subQ2,-1.0]])],"derivedFrom":subQ1}),-1.0]])]});}
            var Q36;
            {var subQ0=sQuery(id+"F0.wireOp",EDGE,"E75.2.20");Q36=makeQuery(id+"F0.imprint","IMPRINT",FACE,{"disambiguationData":[TD([[makeQuery(id+"F0.imprint","IMPRINT",EDGE,{"derivedFrom":subQ0}),-1.0]])]});}
            var Q37;
            {var subQ0=sQuery(id+"F0.wireOp",EDGE,"E25.1.6");var subQ1=sQuery(id+"F0.wireOp",EDGE,"E15");var subQ2=makeQuery(id+"F0.imprint","INTERSECT",VERTEX,{"derivedFrom":[subQ1,subQ0]});Q37=makeQuery(id+"F0.imprint","IMPRINT",FACE,{"disambiguationData":[TD([[makeQuery(id+"F0.imprint","IMPRINT",EDGE,{"disambiguationData":[TD([[subQ2,-1.0]])],"derivedFrom":subQ1}),-1.0]])]});}
            var Q38;
            {var subQ0=sQuery(id+"F0.wireOp",EDGE,"E25.1.6");var subQ1=sQuery(id+"F0.wireOp",EDGE,"E15");var subQ2=makeQuery(id+"F0.imprint","INTERSECT",VERTEX,{"derivedFrom":[subQ1,subQ0]});Q38=makeQuery(id+"F0.imprint","IMPRINT",FACE,{"disambiguationData":[TD([[makeQuery(id+"F0.imprint","IMPRINT",EDGE,{"disambiguationData":[TD([[subQ2,-1.0]])],"derivedFrom":subQ1}),1.0]])]});}
            var Q39;
            {var subQ0=sQuery(id+"F0.wireOp",EDGE,"E75.2.22");Q39=makeQuery(id+"F0.imprint","IMPRINT",FACE,{"disambiguationData":[TD([[makeQuery(id+"F0.imprint","IMPRINT",EDGE,{"derivedFrom":subQ0}),1.0]])]});}
            var Q40;
            {var subQ0=sQuery(id+"F0.wireOp",EDGE,"E75.2.21");var subQ1=sQuery(id+"F0.wireOp",EDGE,"E15");var subQ2=makeQuery(id+"F0.imprint","INTERSECT",VERTEX,{"derivedFrom":[subQ1,subQ0]});Q40=makeQuery(id+"F0.imprint","IMPRINT",FACE,{"disambiguationData":[TD([[makeQuery(id+"F0.imprint","IMPRINT",EDGE,{"disambiguationData":[TD([[subQ2,-1.0]])],"derivedFrom":subQ1}),1.0]])]});}
            var Q41;
            {var subQ0=sQuery(id+"F0.wireOp",EDGE,"E75.2.21");var subQ1=sQuery(id+"F0.wireOp",EDGE,"E15");var subQ2=makeQuery(id+"F0.imprint","INTERSECT",VERTEX,{"derivedFrom":[subQ1,subQ0]});Q41=makeQuery(id+"F0.imprint","IMPRINT",FACE,{"disambiguationData":[TD([[makeQuery(id+"F0.imprint","IMPRINT",EDGE,{"disambiguationData":[TD([[subQ2,-1.0]])],"derivedFrom":subQ1}),-1.0]])]});}
            var Q42;
            {var subQ0=sQuery(id+"F0.wireOp",EDGE,"E75.2.23");Q42=makeQuery(id+"F0.imprint","IMPRINT",FACE,{"disambiguationData":[TD([[makeQuery(id+"F0.imprint","IMPRINT",EDGE,{"derivedFrom":subQ0}),-1.0]])]});}
            var Q43;
            {var subQ0=sQuery(id+"F0.wireOp",EDGE,"E25.1.7");var subQ1=sQuery(id+"F0.wireOp",EDGE,"E15");var subQ2=makeQuery(id+"F0.imprint","INTERSECT",VERTEX,{"derivedFrom":[subQ1,subQ0]});Q43=makeQuery(id+"F0.imprint","IMPRINT",FACE,{"disambiguationData":[TD([[makeQuery(id+"F0.imprint","IMPRINT",EDGE,{"disambiguationData":[TD([[subQ2,-1.0]])],"derivedFrom":subQ1}),-1.0]])]});}
            var Q44;
            {var subQ0=sQuery(id+"F0.wireOp",EDGE,"E25.1.7");var subQ1=sQuery(id+"F0.wireOp",EDGE,"E15");var subQ2=makeQuery(id+"F0.imprint","INTERSECT",VERTEX,{"derivedFrom":[subQ1,subQ0]});Q44=makeQuery(id+"F0.imprint","IMPRINT",FACE,{"disambiguationData":[TD([[makeQuery(id+"F0.imprint","IMPRINT",EDGE,{"disambiguationData":[TD([[subQ2,-1.0]])],"derivedFrom":subQ1}),1.0]])]});}
            var Q45;
            {var subQ0=sQuery(id+"F0.wireOp",EDGE,"E75.2.24");Q45=makeQuery(id+"F0.imprint","IMPRINT",FACE,{"disambiguationData":[TD([[makeQuery(id+"F0.imprint","IMPRINT",EDGE,{"derivedFrom":subQ0}),1.0]])]});}
            var Q46;
            {var subQ1=sQuery(id+"F0.wireOp",EDGE,"E15");var subQ3=sQuery(id+"F0.wireOp",EDGE,"E75.2.25");var subQ4=makeQuery(id+"F0.imprint","INTERSECT",VERTEX,{"derivedFrom":[subQ1,subQ3]});Q46=makeQuery(id+"F0.imprint","IMPRINT",FACE,{"disambiguationData":[TD([[makeQuery(id+"F0.imprint","IMPRINT",EDGE,{"disambiguationData":[TD([[subQ4,-1.0]])],"derivedFrom":subQ3}),-1.0]])]});}
            var Q47;
            {var subQ1=sQuery(id+"F0.wireOp",EDGE,"E15");var subQ3=sQuery(id+"F0.wireOp",EDGE,"E75.2.25");var subQ4=makeQuery(id+"F0.imprint","INTERSECT",VERTEX,{"derivedFrom":[subQ1,subQ3]});Q47=makeQuery(id+"F0.imprint","IMPRINT",FACE,{"disambiguationData":[TD([[makeQuery(id+"F0.imprint","IMPRINT",EDGE,{"disambiguationData":[TD([[subQ4,1.0]])],"derivedFrom":subQ3}),-1.0]])]});}
            var Q48;
            {var subQ0=sQuery(id+"F0.wireOp",EDGE,"E75.2.26");Q48=makeQuery(id+"F0.imprint","IMPRINT",FACE,{"disambiguationData":[TD([[makeQuery(id+"F0.imprint","IMPRINT",EDGE,{"derivedFrom":subQ0}),-1.0]])]});}
            var Q49;
            {var subQ0=sQuery(id+"F0.wireOp",EDGE,"E29");Q49=makeQuery(id+"F0.imprint","IMPRINT",FACE,{"disambiguationData":[TD([[makeQuery(id+"F0.imprint","IMPRINT",EDGE,{"derivedFrom":subQ0}),-1.0]])]});}
            var Q50;
            {var subQ0=sQuery(id+"F0.wireOp",EDGE,"E29");Q50=makeQuery(id+"F0.imprint","IMPRINT",FACE,{"disambiguationData":[TD([[makeQuery(id+"F0.imprint","IMPRINT",EDGE,{"derivedFrom":subQ0}),1.0]])]});}
            var Q51;
            {var subQ0=sQuery(id+"F0.wireOp",EDGE,"E26");var subQ8=makeQuery(id+"F0.imprint","INTERSECT",VERTEX,{"derivedFrom":[subQ0,sQuery(id+"F0.wireOp",EDGE,"E27")]});Q51=makeQuery(id+"F0.imprint","IMPRINT",FACE,{"disambiguationData":[TD([[makeQuery(id+"F0.imprint","IMPRINT",EDGE,{"disambiguationData":[TD([[subQ8,-1.0]])],"derivedFrom":subQ0}),1.0]])]});}
            var Q52;
            {var subQ0=sQuery(id+"F0.wireOp",EDGE,"E27");Q52=makeQuery(id+"F0.imprint","IMPRINT",FACE,{"disambiguationData":[TD([[makeQuery(id+"F0.imprint","IMPRINT",EDGE,{"derivedFrom":subQ0}),1.0]])]});}
            var Q53;
            {var subQ0=sQuery(id+"F0.wireOp",EDGE,"E27");Q53=makeQuery(id+"F0.imprint","IMPRINT",FACE,{"disambiguationData":[TD([[makeQuery(id+"F0.imprint","IMPRINT",EDGE,{"derivedFrom":subQ0}),-1.0]])]});}
            var Q54;
            {var subQ1=sQuery(id+"F0.wireOp",EDGE,"E7");var subQ3=sQuery(id+"F0.wireOp",EDGE,"E48.0");var subQ4=makeQuery(id+"F0.imprint","INTERSECT",VERTEX,{"derivedFrom":[subQ1,subQ3]});Q54=makeQuery(id+"F0.imprint","IMPRINT",FACE,{"disambiguationData":[TD([[makeQuery(id+"F0.imprint","IMPRINT",EDGE,{"disambiguationData":[TD([[subQ4,1.0]])],"derivedFrom":subQ3}),-1.0]])]});}
            var Q55;
            {var subQ1=sQuery(id+"F0.wireOp",EDGE,"E7");var subQ3=sQuery(id+"F0.wireOp",EDGE,"E48.0");var subQ4=makeQuery(id+"F0.imprint","INTERSECT",VERTEX,{"derivedFrom":[subQ1,subQ3]});Q55=makeQuery(id+"F0.imprint","IMPRINT",FACE,{"disambiguationData":[TD([[makeQuery(id+"F0.imprint","IMPRINT",EDGE,{"disambiguationData":[TD([[subQ4,-1.0]])],"derivedFrom":subQ3}),-1.0]])]});}
            var Q56;
            {var subQ0=sQuery(id+"F0.wireOp",EDGE,"E50");Q56=makeQuery(id+"F0.imprint","IMPRINT",FACE,{"disambiguationData":[TD([[makeQuery(id+"F0.imprint","IMPRINT",EDGE,{"derivedFrom":subQ0}),1.0]])]});}
            var Q57;
            {var subQ0=sQuery(id+"F0.wireOp",EDGE,"E25.3.7");var subQ1=sQuery(id+"F0.wireOp",EDGE,"E7");var subQ2=makeQuery(id+"F0.imprint","INTERSECT",VERTEX,{"derivedFrom":[subQ1,subQ0]});Q57=makeQuery(id+"F0.imprint","IMPRINT",FACE,{"disambiguationData":[TD([[makeQuery(id+"F0.imprint","IMPRINT",EDGE,{"disambiguationData":[TD([[subQ2,-1.0]])],"derivedFrom":subQ1}),1.0]])]});}
            var Q58;
            {var subQ0=sQuery(id+"F0.wireOp",EDGE,"E25.3.7");var subQ1=sQuery(id+"F0.wireOp",EDGE,"E7");var subQ2=makeQuery(id+"F0.imprint","INTERSECT",VERTEX,{"derivedFrom":[subQ1,subQ0]});Q58=makeQuery(id+"F0.imprint","IMPRINT",FACE,{"disambiguationData":[TD([[makeQuery(id+"F0.imprint","IMPRINT",EDGE,{"disambiguationData":[TD([[subQ2,-1.0]])],"derivedFrom":subQ1}),-1.0]])]});}
            var Q59;
            {var subQ0=sQuery(id+"F0.wireOp",EDGE,"E52");Q59=makeQuery(id+"F0.imprint","IMPRINT",FACE,{"disambiguationData":[TD([[makeQuery(id+"F0.imprint","IMPRINT",EDGE,{"derivedFrom":subQ0}),-1.0]])]});}
            var Q60;
            {var subQ0=sQuery(id+"F0.wireOp",EDGE,"E51.0");var subQ1=sQuery(id+"F0.wireOp",EDGE,"E7");var subQ2=makeQuery(id+"F0.imprint","INTERSECT",VERTEX,{"derivedFrom":[subQ1,subQ0]});Q60=makeQuery(id+"F0.imprint","IMPRINT",FACE,{"disambiguationData":[TD([[makeQuery(id+"F0.imprint","IMPRINT",EDGE,{"disambiguationData":[TD([[subQ2,-1.0]])],"derivedFrom":subQ1}),-1.0]])]});}
            var Q61;
            {var subQ0=sQuery(id+"F0.wireOp",EDGE,"E51.0");var subQ1=sQuery(id+"F0.wireOp",EDGE,"E7");var subQ2=makeQuery(id+"F0.imprint","INTERSECT",VERTEX,{"derivedFrom":[subQ1,subQ0]});Q61=makeQuery(id+"F0.imprint","IMPRINT",FACE,{"disambiguationData":[TD([[makeQuery(id+"F0.imprint","IMPRINT",EDGE,{"disambiguationData":[TD([[subQ2,-1.0]])],"derivedFrom":subQ1}),1.0]])]});}
            var Q62;
            {var subQ0=sQuery(id+"F0.wireOp",EDGE,"E53");Q62=makeQuery(id+"F0.imprint","IMPRINT",FACE,{"disambiguationData":[TD([[makeQuery(id+"F0.imprint","IMPRINT",EDGE,{"derivedFrom":subQ0}),1.0]])]});}
            var Q63;
            {var subQ0=sQuery(id+"F0.wireOp",EDGE,"E25.3.6");var subQ1=sQuery(id+"F0.wireOp",EDGE,"E7");var subQ2=makeQuery(id+"F0.imprint","INTERSECT",VERTEX,{"derivedFrom":[subQ1,subQ0]});Q63=makeQuery(id+"F0.imprint","IMPRINT",FACE,{"disambiguationData":[TD([[makeQuery(id+"F0.imprint","IMPRINT",EDGE,{"disambiguationData":[TD([[subQ2,-1.0]])],"derivedFrom":subQ1}),1.0]])]});}
            var Q64;
            {var subQ0=sQuery(id+"F0.wireOp",EDGE,"E25.3.6");var subQ1=sQuery(id+"F0.wireOp",EDGE,"E7");var subQ2=makeQuery(id+"F0.imprint","INTERSECT",VERTEX,{"derivedFrom":[subQ1,subQ0]});Q64=makeQuery(id+"F0.imprint","IMPRINT",FACE,{"disambiguationData":[TD([[makeQuery(id+"F0.imprint","IMPRINT",EDGE,{"disambiguationData":[TD([[subQ2,-1.0]])],"derivedFrom":subQ1}),-1.0]])]});}
            var Q65;
            {var subQ0=sQuery(id+"F0.wireOp",EDGE,"E55");Q65=makeQuery(id+"F0.imprint","IMPRINT",FACE,{"disambiguationData":[TD([[makeQuery(id+"F0.imprint","IMPRINT",EDGE,{"derivedFrom":subQ0}),-1.0]])]});}
            var Q66;
            {var subQ0=sQuery(id+"F0.wireOp",EDGE,"E54.0");var subQ1=sQuery(id+"F0.wireOp",EDGE,"E7");var subQ2=makeQuery(id+"F0.imprint","INTERSECT",VERTEX,{"derivedFrom":[subQ1,subQ0]});Q66=makeQuery(id+"F0.imprint","IMPRINT",FACE,{"disambiguationData":[TD([[makeQuery(id+"F0.imprint","IMPRINT",EDGE,{"disambiguationData":[TD([[subQ2,-1.0]])],"derivedFrom":subQ1}),-1.0]])]});}
            var Q67;
            {var subQ0=sQuery(id+"F0.wireOp",EDGE,"E54.0");var subQ1=sQuery(id+"F0.wireOp",EDGE,"E7");var subQ2=makeQuery(id+"F0.imprint","INTERSECT",VERTEX,{"derivedFrom":[subQ1,subQ0]});Q67=makeQuery(id+"F0.imprint","IMPRINT",FACE,{"disambiguationData":[TD([[makeQuery(id+"F0.imprint","IMPRINT",EDGE,{"disambiguationData":[TD([[subQ2,-1.0]])],"derivedFrom":subQ1}),1.0]])]});}
            var Q68;
            {var subQ0=sQuery(id+"F0.wireOp",EDGE,"E56");Q68=makeQuery(id+"F0.imprint","IMPRINT",FACE,{"disambiguationData":[TD([[makeQuery(id+"F0.imprint","IMPRINT",EDGE,{"derivedFrom":subQ0}),1.0]])]});}
            var Q69;
            {var subQ0=sQuery(id+"F0.wireOp",EDGE,"E25.3.5");var subQ1=sQuery(id+"F0.wireOp",EDGE,"E7");var subQ2=makeQuery(id+"F0.imprint","INTERSECT",VERTEX,{"derivedFrom":[subQ1,subQ0]});Q69=makeQuery(id+"F0.imprint","IMPRINT",FACE,{"disambiguationData":[TD([[makeQuery(id+"F0.imprint","IMPRINT",EDGE,{"disambiguationData":[TD([[subQ2,-1.0]])],"derivedFrom":subQ1}),1.0]])]});}
            var Q70;
            {var subQ0=sQuery(id+"F0.wireOp",EDGE,"E25.3.5");var subQ1=sQuery(id+"F0.wireOp",EDGE,"E7");var subQ2=makeQuery(id+"F0.imprint","INTERSECT",VERTEX,{"derivedFrom":[subQ1,subQ0]});Q70=makeQuery(id+"F0.imprint","IMPRINT",FACE,{"disambiguationData":[TD([[makeQuery(id+"F0.imprint","IMPRINT",EDGE,{"disambiguationData":[TD([[subQ2,-1.0]])],"derivedFrom":subQ1}),-1.0]])]});}
            var Q71;
            {var subQ0=sQuery(id+"F0.wireOp",EDGE,"E58");Q71=makeQuery(id+"F0.imprint","IMPRINT",FACE,{"disambiguationData":[TD([[makeQuery(id+"F0.imprint","IMPRINT",EDGE,{"derivedFrom":subQ0}),1.0]])]});}
            var Q72;
            {var subQ0=sQuery(id+"F0.wireOp",EDGE,"E57.0");var subQ1=sQuery(id+"F0.wireOp",EDGE,"E7");var subQ2=makeQuery(id+"F0.imprint","INTERSECT",VERTEX,{"derivedFrom":[subQ1,subQ0]});Q72=makeQuery(id+"F0.imprint","IMPRINT",FACE,{"disambiguationData":[TD([[makeQuery(id+"F0.imprint","IMPRINT",EDGE,{"disambiguationData":[TD([[subQ2,-1.0]])],"derivedFrom":subQ1}),-1.0]])]});}
            var Q73;
            {var subQ0=sQuery(id+"F0.wireOp",EDGE,"E57.0");var subQ1=sQuery(id+"F0.wireOp",EDGE,"E7");var subQ2=makeQuery(id+"F0.imprint","INTERSECT",VERTEX,{"derivedFrom":[subQ1,subQ0]});Q73=makeQuery(id+"F0.imprint","IMPRINT",FACE,{"disambiguationData":[TD([[makeQuery(id+"F0.imprint","IMPRINT",EDGE,{"disambiguationData":[TD([[subQ2,-1.0]])],"derivedFrom":subQ1}),1.0]])]});}
            var Q74;
            {var subQ0=sQuery(id+"F0.wireOp",EDGE,"E59");Q74=makeQuery(id+"F0.imprint","IMPRINT",FACE,{"disambiguationData":[TD([[makeQuery(id+"F0.imprint","IMPRINT",EDGE,{"derivedFrom":subQ0}),-1.0]])]});}
            var Q75;
            {var subQ0=sQuery(id+"F0.wireOp",EDGE,"E25.3.4");var subQ1=sQuery(id+"F0.wireOp",EDGE,"E7");var subQ2=makeQuery(id+"F0.imprint","INTERSECT",VERTEX,{"derivedFrom":[subQ1,subQ0]});Q75=makeQuery(id+"F0.imprint","IMPRINT",FACE,{"disambiguationData":[TD([[makeQuery(id+"F0.imprint","IMPRINT",EDGE,{"disambiguationData":[TD([[subQ2,-1.0]])],"derivedFrom":subQ1}),1.0]])]});}
            var Q76;
            {var subQ0=sQuery(id+"F0.wireOp",EDGE,"E25.3.4");var subQ1=sQuery(id+"F0.wireOp",EDGE,"E7");var subQ2=makeQuery(id+"F0.imprint","INTERSECT",VERTEX,{"derivedFrom":[subQ1,subQ0]});Q76=makeQuery(id+"F0.imprint","IMPRINT",FACE,{"disambiguationData":[TD([[makeQuery(id+"F0.imprint","IMPRINT",EDGE,{"disambiguationData":[TD([[subQ2,-1.0]])],"derivedFrom":subQ1}),-1.0]])]});}
            var Q77;
            {var subQ0=sQuery(id+"F0.wireOp",EDGE,"E60.0");var subQ1=sQuery(id+"F0.wireOp",EDGE,"E7");var subQ2=makeQuery(id+"F0.imprint","INTERSECT",VERTEX,{"derivedFrom":[subQ1,subQ0]});Q77=makeQuery(id+"F0.imprint","IMPRINT",FACE,{"disambiguationData":[TD([[makeQuery(id+"F0.imprint","IMPRINT",EDGE,{"disambiguationData":[TD([[subQ2,-1.0]])],"derivedFrom":subQ1}),-1.0]])]});}
            var Q78;
            {var subQ0=sQuery(id+"F0.wireOp",EDGE,"E60.0");var subQ1=sQuery(id+"F0.wireOp",EDGE,"E7");var subQ2=makeQuery(id+"F0.imprint","INTERSECT",VERTEX,{"derivedFrom":[subQ1,subQ0]});Q78=makeQuery(id+"F0.imprint","IMPRINT",FACE,{"disambiguationData":[TD([[makeQuery(id+"F0.imprint","IMPRINT",EDGE,{"disambiguationData":[TD([[subQ2,-1.0]])],"derivedFrom":subQ1}),1.0]])]});}
            var Q79;
            {var subQ0=sQuery(id+"F0.wireOp",EDGE,"E62");Q79=makeQuery(id+"F0.imprint","IMPRINT",FACE,{"disambiguationData":[TD([[makeQuery(id+"F0.imprint","IMPRINT",EDGE,{"derivedFrom":subQ0}),-1.0]])]});}
            var Q80;
            {var subQ0=sQuery(id+"F0.wireOp",EDGE,"E25.3.3");var subQ1=sQuery(id+"F0.wireOp",EDGE,"E7");var subQ2=makeQuery(id+"F0.imprint","INTERSECT",VERTEX,{"derivedFrom":[subQ1,subQ0]});Q80=makeQuery(id+"F0.imprint","IMPRINT",FACE,{"disambiguationData":[TD([[makeQuery(id+"F0.imprint","IMPRINT",EDGE,{"disambiguationData":[TD([[subQ2,-1.0]])],"derivedFrom":subQ1}),1.0]])]});}
            var Q81;
            {var subQ0=sQuery(id+"F0.wireOp",EDGE,"E25.3.3");var subQ1=sQuery(id+"F0.wireOp",EDGE,"E7");var subQ2=makeQuery(id+"F0.imprint","INTERSECT",VERTEX,{"derivedFrom":[subQ1,subQ0]});Q81=makeQuery(id+"F0.imprint","IMPRINT",FACE,{"disambiguationData":[TD([[makeQuery(id+"F0.imprint","IMPRINT",EDGE,{"disambiguationData":[TD([[subQ2,-1.0]])],"derivedFrom":subQ1}),-1.0]])]});}
            var Q82;
            {var subQ0=sQuery(id+"F0.wireOp",EDGE,"E64");Q82=makeQuery(id+"F0.imprint","IMPRINT",FACE,{"disambiguationData":[TD([[makeQuery(id+"F0.imprint","IMPRINT",EDGE,{"derivedFrom":subQ0}),1.0]])]});}
            var Q83;
            {var subQ0=sQuery(id+"F0.wireOp",EDGE,"E63.0");var subQ1=sQuery(id+"F0.wireOp",EDGE,"E7");var subQ2=makeQuery(id+"F0.imprint","INTERSECT",VERTEX,{"derivedFrom":[subQ1,subQ0]});Q83=makeQuery(id+"F0.imprint","IMPRINT",FACE,{"disambiguationData":[TD([[makeQuery(id+"F0.imprint","IMPRINT",EDGE,{"disambiguationData":[TD([[subQ2,-1.0]])],"derivedFrom":subQ1}),-1.0]])]});}
            var Q84;
            {var subQ0=sQuery(id+"F0.wireOp",EDGE,"E61");Q84=makeQuery(id+"F0.imprint","IMPRINT",FACE,{"disambiguationData":[TD([[makeQuery(id+"F0.imprint","IMPRINT",EDGE,{"derivedFrom":subQ0}),1.0]])]});}
            var Q85;
            {var subQ0=sQuery(id+"F0.wireOp",EDGE,"E49");Q85=makeQuery(id+"F0.imprint","IMPRINT",FACE,{"disambiguationData":[TD([[makeQuery(id+"F0.imprint","IMPRINT",EDGE,{"derivedFrom":subQ0}),-1.0]])]});}
            var Q86;
            {var subQ0=sQuery(id+"F0.wireOp",EDGE,"E63.0");var subQ1=sQuery(id+"F0.wireOp",EDGE,"E7");var subQ2=makeQuery(id+"F0.imprint","INTERSECT",VERTEX,{"derivedFrom":[subQ1,subQ0]});Q86=makeQuery(id+"F0.imprint","IMPRINT",FACE,{"disambiguationData":[TD([[makeQuery(id+"F0.imprint","IMPRINT",EDGE,{"disambiguationData":[TD([[subQ2,-1.0]])],"derivedFrom":subQ1}),1.0]])]});}
            var Q87;
            {var subQ0=sQuery(id+"F0.wireOp",EDGE,"E65");Q87=makeQuery(id+"F0.imprint","IMPRINT",FACE,{"disambiguationData":[TD([[makeQuery(id+"F0.imprint","IMPRINT",EDGE,{"derivedFrom":subQ0}),-1.0]])]});}
            var Q88;
            {var subQ0=sQuery(id+"F0.wireOp",EDGE,"E25.3.2");var subQ1=sQuery(id+"F0.wireOp",EDGE,"E7");var subQ2=makeQuery(id+"F0.imprint","INTERSECT",VERTEX,{"derivedFrom":[subQ1,subQ0]});Q88=makeQuery(id+"F0.imprint","IMPRINT",FACE,{"disambiguationData":[TD([[makeQuery(id+"F0.imprint","IMPRINT",EDGE,{"disambiguationData":[TD([[subQ2,-1.0]])],"derivedFrom":subQ1}),-1.0]])]});}
            var Q89;
            {var subQ0=sQuery(id+"F0.wireOp",EDGE,"E25.3.2");var subQ1=sQuery(id+"F0.wireOp",EDGE,"E7");var subQ2=makeQuery(id+"F0.imprint","INTERSECT",VERTEX,{"derivedFrom":[subQ1,subQ0]});Q89=makeQuery(id+"F0.imprint","IMPRINT",FACE,{"disambiguationData":[TD([[makeQuery(id+"F0.imprint","IMPRINT",EDGE,{"disambiguationData":[TD([[subQ2,-1.0]])],"derivedFrom":subQ1}),1.0]])]});}
            var Q90;
            {var subQ0=sQuery(id+"F0.wireOp",EDGE,"E66.0");var subQ1=sQuery(id+"F0.wireOp",EDGE,"E7");var subQ2=makeQuery(id+"F0.imprint","INTERSECT",VERTEX,{"derivedFrom":[subQ1,subQ0]});Q90=makeQuery(id+"F0.imprint","IMPRINT",FACE,{"disambiguationData":[TD([[makeQuery(id+"F0.imprint","IMPRINT",EDGE,{"disambiguationData":[TD([[subQ2,-1.0]])],"derivedFrom":subQ1}),1.0]])]});}
            var Q91;
            {var subQ0=sQuery(id+"F0.wireOp",EDGE,"E66.0");var subQ1=sQuery(id+"F0.wireOp",EDGE,"E7");var subQ2=makeQuery(id+"F0.imprint","INTERSECT",VERTEX,{"derivedFrom":[subQ1,subQ0]});Q91=makeQuery(id+"F0.imprint","IMPRINT",FACE,{"disambiguationData":[TD([[makeQuery(id+"F0.imprint","IMPRINT",EDGE,{"disambiguationData":[TD([[subQ2,-1.0]])],"derivedFrom":subQ1}),-1.0]])]});}
            var Q92;
            {var subQ0=sQuery(id+"F0.wireOp",EDGE,"E67");Q92=makeQuery(id+"F0.imprint","IMPRINT",FACE,{"disambiguationData":[TD([[makeQuery(id+"F0.imprint","IMPRINT",EDGE,{"derivedFrom":subQ0}),1.0]])]});}
            var Q93;
            {var subQ0=sQuery(id+"F0.wireOp",EDGE,"E68");Q93=makeQuery(id+"F0.imprint","IMPRINT",FACE,{"disambiguationData":[TD([[makeQuery(id+"F0.imprint","IMPRINT",EDGE,{"derivedFrom":subQ0}),-1.0]])]});}
            var Q94;
            {var subQ0=sQuery(id+"F0.wireOp",EDGE,"E25.3.1");var subQ1=sQuery(id+"F0.wireOp",EDGE,"E7");var subQ2=makeQuery(id+"F0.imprint","INTERSECT",VERTEX,{"derivedFrom":[subQ1,subQ0]});Q94=makeQuery(id+"F0.imprint","IMPRINT",FACE,{"disambiguationData":[TD([[makeQuery(id+"F0.imprint","IMPRINT",EDGE,{"disambiguationData":[TD([[subQ2,-1.0]])],"derivedFrom":subQ1}),1.0]])]});}
            var Q95;
            {var subQ0=sQuery(id+"F0.wireOp",EDGE,"E25.3.1");var subQ1=sQuery(id+"F0.wireOp",EDGE,"E7");var subQ2=makeQuery(id+"F0.imprint","INTERSECT",VERTEX,{"derivedFrom":[subQ1,subQ0]});Q95=makeQuery(id+"F0.imprint","IMPRINT",FACE,{"disambiguationData":[TD([[makeQuery(id+"F0.imprint","IMPRINT",EDGE,{"disambiguationData":[TD([[subQ2,-1.0]])],"derivedFrom":subQ1}),-1.0]])]});}
            var Q96;
            {var subQ0=sQuery(id+"F0.wireOp",EDGE,"E70");Q96=makeQuery(id+"F0.imprint","IMPRINT",FACE,{"disambiguationData":[TD([[makeQuery(id+"F0.imprint","IMPRINT",EDGE,{"derivedFrom":subQ0}),1.0]])]});}
            var Q97;
            {var subQ0=sQuery(id+"F0.wireOp",EDGE,"E69.0");var subQ1=sQuery(id+"F0.wireOp",EDGE,"E7");var subQ2=makeQuery(id+"F0.imprint","INTERSECT",VERTEX,{"derivedFrom":[subQ1,subQ0]});Q97=makeQuery(id+"F0.imprint","IMPRINT",FACE,{"disambiguationData":[TD([[makeQuery(id+"F0.imprint","IMPRINT",EDGE,{"disambiguationData":[TD([[subQ2,-1.0]])],"derivedFrom":subQ1}),1.0]])]});}
            var Q98;
            {var subQ0=sQuery(id+"F0.wireOp",EDGE,"E71");Q98=makeQuery(id+"F0.imprint","IMPRINT",FACE,{"disambiguationData":[TD([[makeQuery(id+"F0.imprint","IMPRINT",EDGE,{"derivedFrom":subQ0}),-1.0]])]});}
            var Q99;
            {var subQ0=sQuery(id+"F0.wireOp",EDGE,"E25.3.0");var subQ1=sQuery(id+"F0.wireOp",EDGE,"E7");var subQ2=makeQuery(id+"F0.imprint","INTERSECT",VERTEX,{"derivedFrom":[subQ1,subQ0]});Q99=makeQuery(id+"F0.imprint","IMPRINT",FACE,{"disambiguationData":[TD([[makeQuery(id+"F0.imprint","IMPRINT",EDGE,{"disambiguationData":[TD([[subQ2,-1.0]])],"derivedFrom":subQ1}),1.0]])]});}
            var Q100;
            {var subQ0=sQuery(id+"F0.wireOp",EDGE,"E25.3.0");var subQ1=sQuery(id+"F0.wireOp",EDGE,"E7");var subQ2=makeQuery(id+"F0.imprint","INTERSECT",VERTEX,{"derivedFrom":[subQ1,subQ0]});Q100=makeQuery(id+"F0.imprint","IMPRINT",FACE,{"disambiguationData":[TD([[makeQuery(id+"F0.imprint","IMPRINT",EDGE,{"disambiguationData":[TD([[subQ2,-1.0]])],"derivedFrom":subQ1}),-1.0]])]});}
            var Q101;
            Q101=makeQuery(id+"F0.imprint","IMPRINT",FACE,{"disambiguationData":[TD([[makeQuery(id+"F0.imprint","IMPRINT",EDGE,{"derivedFrom":sQuery(id+"F0.wireOp",EDGE,"E72.0")}),-1.0]])]});
            var Q102;
            {var subQ0=sQuery(id+"F0.wireOp",EDGE,"E69.0");var subQ1=sQuery(id+"F0.wireOp",EDGE,"E7");var subQ2=makeQuery(id+"F0.imprint","INTERSECT",VERTEX,{"derivedFrom":[subQ1,subQ0]});Q102=makeQuery(id+"F0.imprint","IMPRINT",FACE,{"disambiguationData":[TD([[makeQuery(id+"F0.imprint","IMPRINT",EDGE,{"disambiguationData":[TD([[subQ2,-1.0]])],"derivedFrom":subQ1}),-1.0]])]});}
            extrude(context, id + "F2", {"entities" : qUnion([Q0, Q1, Q2, Q3, Q4, Q5, Q6, Q7, Q8, Q9, Q10, Q11, Q12, Q13, Q14, Q15, Q16, Q17, Q18, Q19, Q20, Q21, Q22, Q23, Q24, Q25, Q26, Q27, Q28, Q29, Q30, Q31, Q32, Q33, Q34, Q35, Q36, Q37, Q38, Q39, Q40, Q41, Q42, Q43, Q44, Q45, Q46, Q47, Q48, Q49, Q50, Q51, Q52, Q53, Q54, Q55, Q56, Q57, Q58, Q59, Q60, Q61, Q62, Q63, Q64, Q65, Q66, Q67, Q68, Q69, Q70, Q71, Q72, Q73, Q74, Q75, Q76, Q77, Q78, Q79, Q80, Q81, Q82, Q83, Q84, Q85, Q86, Q87, Q88, Q89, Q90, Q91, Q92, Q93, Q94, Q95, Q96, Q97, Q98, Q99, Q100, Q101, Q102]), "depth" : 12.7 * mm});
        }
        {
            var Q0;
            {var subQ0=sQuery(id+"F0.wireOp",EDGE,"E28");Q0=makeQuery(id+"F0.imprint","IMPRINT",FACE,{"disambiguationData":[TD([[makeQuery(id+"F0.imprint","IMPRINT",EDGE,{"derivedFrom":subQ0}),-1.0]])]});}
            var Q1;
            {var subQ0=sQuery(id+"F0.wireOp",EDGE,"E28");Q1=makeQuery(id+"F0.imprint","IMPRINT",FACE,{"disambiguationData":[TD([[makeQuery(id+"F0.imprint","IMPRINT",EDGE,{"derivedFrom":subQ0}),1.0]])]});}
            var Q2;
            {var subQ0=sQuery(id+"F0.wireOp",EDGE,"E75.1.24");Q2=makeQuery(id+"F0.imprint","IMPRINT",FACE,{"disambiguationData":[TD([[makeQuery(id+"F0.imprint","IMPRINT",EDGE,{"derivedFrom":subQ0}),1.0]])]});}
            var Q3;
            {var subQ1=sQuery(id+"F0.wireOp",EDGE,"E0");var subQ3=sQuery(id+"F0.wireOp",EDGE,"E75.1.25");var subQ4=makeQuery(id+"F0.imprint","INTERSECT",VERTEX,{"derivedFrom":[subQ1,subQ3]});Q3=makeQuery(id+"F0.imprint","IMPRINT",FACE,{"disambiguationData":[TD([[makeQuery(id+"F0.imprint","IMPRINT",EDGE,{"disambiguationData":[TD([[subQ4,-1.0]])],"derivedFrom":subQ3}),-1.0]])]});}
            var Q4;
            {var subQ1=sQuery(id+"F0.wireOp",EDGE,"E0");var subQ3=sQuery(id+"F0.wireOp",EDGE,"E75.1.25");var subQ4=makeQuery(id+"F0.imprint","INTERSECT",VERTEX,{"derivedFrom":[subQ1,subQ3]});Q4=makeQuery(id+"F0.imprint","IMPRINT",FACE,{"disambiguationData":[TD([[makeQuery(id+"F0.imprint","IMPRINT",EDGE,{"disambiguationData":[TD([[subQ4,1.0]])],"derivedFrom":subQ3}),-1.0]])]});}
            var Q5;
            {var subQ0=sQuery(id+"F0.wireOp",EDGE,"E75.1.26");Q5=makeQuery(id+"F0.imprint","IMPRINT",FACE,{"disambiguationData":[TD([[makeQuery(id+"F0.imprint","IMPRINT",EDGE,{"derivedFrom":subQ0}),-1.0]])]});}
            var Q6;
            {var subQ0=sQuery(id+"F0.wireOp",EDGE,"E75.1.25");var subQ1=sQuery(id+"F0.wireOp",EDGE,"E0");var subQ2=makeQuery(id+"F0.imprint","INTERSECT",VERTEX,{"derivedFrom":[subQ1,subQ0]});Q6=makeQuery(id+"F0.imprint","IMPRINT",FACE,{"disambiguationData":[TD([[makeQuery(id+"F0.imprint","IMPRINT",EDGE,{"disambiguationData":[TD([[subQ2,-1.0]])],"derivedFrom":subQ1}),1.0]])]});}
            var Q7;
            {var subQ0=sQuery(id+"F0.wireOp",EDGE,"E75.1.25");var subQ1=sQuery(id+"F0.wireOp",EDGE,"E0");var subQ2=makeQuery(id+"F0.imprint","INTERSECT",VERTEX,{"derivedFrom":[subQ1,subQ0]});Q7=makeQuery(id+"F0.imprint","IMPRINT",FACE,{"disambiguationData":[TD([[makeQuery(id+"F0.imprint","IMPRINT",EDGE,{"disambiguationData":[TD([[subQ2,-1.0]])],"derivedFrom":subQ1}),-1.0]])]});}
            var Q8;
            {var subQ0=sQuery(id+"F0.wireOp",EDGE,"E75.1.22");Q8=makeQuery(id+"F0.imprint","IMPRINT",FACE,{"disambiguationData":[TD([[makeQuery(id+"F0.imprint","IMPRINT",EDGE,{"derivedFrom":subQ0}),1.0]])]});}
            var Q9;
            {var subQ0=sQuery(id+"F0.wireOp",EDGE,"E17.0");var subQ1=sQuery(id+"F0.wireOp",EDGE,"E0");var subQ2=makeQuery(id+"F0.imprint","INTERSECT",VERTEX,{"derivedFrom":[subQ1,subQ0]});Q9=makeQuery(id+"F0.imprint","IMPRINT",FACE,{"disambiguationData":[TD([[makeQuery(id+"F0.imprint","IMPRINT",EDGE,{"disambiguationData":[TD([[subQ2,-1.0]])],"derivedFrom":subQ1}),1.0]])]});}
            var Q10;
            {var subQ0=sQuery(id+"F0.wireOp",EDGE,"E75.1.23");Q10=makeQuery(id+"F0.imprint","IMPRINT",FACE,{"disambiguationData":[TD([[makeQuery(id+"F0.imprint","IMPRINT",EDGE,{"derivedFrom":subQ0}),-1.0]])]});}
            var Q11;
            {var subQ0=sQuery(id+"F0.wireOp",EDGE,"E75.1.21");var subQ1=sQuery(id+"F0.wireOp",EDGE,"E0");var subQ2=makeQuery(id+"F0.imprint","INTERSECT",VERTEX,{"derivedFrom":[subQ1,subQ0]});Q11=makeQuery(id+"F0.imprint","IMPRINT",FACE,{"disambiguationData":[TD([[makeQuery(id+"F0.imprint","IMPRINT",EDGE,{"disambiguationData":[TD([[subQ2,-1.0]])],"derivedFrom":subQ1}),1.0]])]});}
            var Q12;
            {var subQ0=sQuery(id+"F0.wireOp",EDGE,"E75.1.21");var subQ1=sQuery(id+"F0.wireOp",EDGE,"E0");var subQ2=makeQuery(id+"F0.imprint","INTERSECT",VERTEX,{"derivedFrom":[subQ1,subQ0]});Q12=makeQuery(id+"F0.imprint","IMPRINT",FACE,{"disambiguationData":[TD([[makeQuery(id+"F0.imprint","IMPRINT",EDGE,{"disambiguationData":[TD([[subQ2,-1.0]])],"derivedFrom":subQ1}),-1.0]])]});}
            var Q13;
            {var subQ0=sQuery(id+"F0.wireOp",EDGE,"E17.0");var subQ1=sQuery(id+"F0.wireOp",EDGE,"E0");var subQ2=makeQuery(id+"F0.imprint","INTERSECT",VERTEX,{"derivedFrom":[subQ1,subQ0]});Q13=makeQuery(id+"F0.imprint","IMPRINT",FACE,{"disambiguationData":[TD([[makeQuery(id+"F0.imprint","IMPRINT",EDGE,{"disambiguationData":[TD([[subQ2,-1.0]])],"derivedFrom":subQ1}),-1.0]])]});}
            var Q14;
            {var subQ0=sQuery(id+"F0.wireOp",EDGE,"E75.1.19");Q14=makeQuery(id+"F0.imprint","IMPRINT",FACE,{"disambiguationData":[TD([[makeQuery(id+"F0.imprint","IMPRINT",EDGE,{"derivedFrom":subQ0}),1.0]])]});}
            var Q15;
            {var subQ0=sQuery(id+"F0.wireOp",EDGE,"E18.0");var subQ1=sQuery(id+"F0.wireOp",EDGE,"E0");var subQ2=makeQuery(id+"F0.imprint","INTERSECT",VERTEX,{"derivedFrom":[subQ1,subQ0]});Q15=makeQuery(id+"F0.imprint","IMPRINT",FACE,{"disambiguationData":[TD([[makeQuery(id+"F0.imprint","IMPRINT",EDGE,{"disambiguationData":[TD([[subQ2,-1.0]])],"derivedFrom":subQ1}),-1.0]])]});}
            var Q16;
            {var subQ0=sQuery(id+"F0.wireOp",EDGE,"E18.0");var subQ1=sQuery(id+"F0.wireOp",EDGE,"E0");var subQ2=makeQuery(id+"F0.imprint","INTERSECT",VERTEX,{"derivedFrom":[subQ1,subQ0]});Q16=makeQuery(id+"F0.imprint","IMPRINT",FACE,{"disambiguationData":[TD([[makeQuery(id+"F0.imprint","IMPRINT",EDGE,{"disambiguationData":[TD([[subQ2,-1.0]])],"derivedFrom":subQ1}),1.0]])]});}
            var Q17;
            {var subQ0=sQuery(id+"F0.wireOp",EDGE,"E75.1.20");Q17=makeQuery(id+"F0.imprint","IMPRINT",FACE,{"disambiguationData":[TD([[makeQuery(id+"F0.imprint","IMPRINT",EDGE,{"derivedFrom":subQ0}),-1.0]])]});}
            var Q18;
            {var subQ0=sQuery(id+"F0.wireOp",EDGE,"E75.1.18");var subQ1=sQuery(id+"F0.wireOp",EDGE,"E0");var subQ2=makeQuery(id+"F0.imprint","INTERSECT",VERTEX,{"derivedFrom":[subQ1,subQ0]});Q18=makeQuery(id+"F0.imprint","IMPRINT",FACE,{"disambiguationData":[TD([[makeQuery(id+"F0.imprint","IMPRINT",EDGE,{"disambiguationData":[TD([[subQ2,-1.0]])],"derivedFrom":subQ1}),1.0]])]});}
            var Q19;
            {var subQ0=sQuery(id+"F0.wireOp",EDGE,"E75.1.18");var subQ1=sQuery(id+"F0.wireOp",EDGE,"E0");var subQ2=makeQuery(id+"F0.imprint","INTERSECT",VERTEX,{"derivedFrom":[subQ1,subQ0]});Q19=makeQuery(id+"F0.imprint","IMPRINT",FACE,{"disambiguationData":[TD([[makeQuery(id+"F0.imprint","IMPRINT",EDGE,{"disambiguationData":[TD([[subQ2,-1.0]])],"derivedFrom":subQ1}),-1.0]])]});}
            var Q20;
            {var subQ0=sQuery(id+"F0.wireOp",EDGE,"E75.1.16");Q20=makeQuery(id+"F0.imprint","IMPRINT",FACE,{"disambiguationData":[TD([[makeQuery(id+"F0.imprint","IMPRINT",EDGE,{"derivedFrom":subQ0}),1.0]])]});}
            var Q21;
            {var subQ0=sQuery(id+"F0.wireOp",EDGE,"E19.0");var subQ1=sQuery(id+"F0.wireOp",EDGE,"E0");var subQ2=makeQuery(id+"F0.imprint","INTERSECT",VERTEX,{"derivedFrom":[subQ1,subQ0]});Q21=makeQuery(id+"F0.imprint","IMPRINT",FACE,{"disambiguationData":[TD([[makeQuery(id+"F0.imprint","IMPRINT",EDGE,{"disambiguationData":[TD([[subQ2,-1.0]])],"derivedFrom":subQ1}),1.0]])]});}
            var Q22;
            {var subQ0=sQuery(id+"F0.wireOp",EDGE,"E19.0");var subQ1=sQuery(id+"F0.wireOp",EDGE,"E0");var subQ2=makeQuery(id+"F0.imprint","INTERSECT",VERTEX,{"derivedFrom":[subQ1,subQ0]});Q22=makeQuery(id+"F0.imprint","IMPRINT",FACE,{"disambiguationData":[TD([[makeQuery(id+"F0.imprint","IMPRINT",EDGE,{"disambiguationData":[TD([[subQ2,-1.0]])],"derivedFrom":subQ1}),-1.0]])]});}
            var Q23;
            {var subQ0=sQuery(id+"F0.wireOp",EDGE,"E75.1.17");Q23=makeQuery(id+"F0.imprint","IMPRINT",FACE,{"disambiguationData":[TD([[makeQuery(id+"F0.imprint","IMPRINT",EDGE,{"derivedFrom":subQ0}),-1.0]])]});}
            var Q24;
            {var subQ0=sQuery(id+"F0.wireOp",EDGE,"E75.1.15");var subQ1=sQuery(id+"F0.wireOp",EDGE,"E0");var subQ2=makeQuery(id+"F0.imprint","INTERSECT",VERTEX,{"derivedFrom":[subQ1,subQ0]});Q24=makeQuery(id+"F0.imprint","IMPRINT",FACE,{"disambiguationData":[TD([[makeQuery(id+"F0.imprint","IMPRINT",EDGE,{"disambiguationData":[TD([[subQ2,-1.0]])],"derivedFrom":subQ1}),1.0]])]});}
            var Q25;
            {var subQ0=sQuery(id+"F0.wireOp",EDGE,"E75.1.15");var subQ1=sQuery(id+"F0.wireOp",EDGE,"E0");var subQ2=makeQuery(id+"F0.imprint","INTERSECT",VERTEX,{"derivedFrom":[subQ1,subQ0]});Q25=makeQuery(id+"F0.imprint","IMPRINT",FACE,{"disambiguationData":[TD([[makeQuery(id+"F0.imprint","IMPRINT",EDGE,{"disambiguationData":[TD([[subQ2,-1.0]])],"derivedFrom":subQ1}),-1.0]])]});}
            var Q26;
            {var subQ0=sQuery(id+"F0.wireOp",EDGE,"E75.1.14");Q26=makeQuery(id+"F0.imprint","IMPRINT",FACE,{"disambiguationData":[TD([[makeQuery(id+"F0.imprint","IMPRINT",EDGE,{"derivedFrom":subQ0}),1.0]])]});}
            var Q27;
            {var subQ0=sQuery(id+"F0.wireOp",EDGE,"E20.0");var subQ1=sQuery(id+"F0.wireOp",EDGE,"E0");var subQ2=makeQuery(id+"F0.imprint","INTERSECT",VERTEX,{"derivedFrom":[subQ1,subQ0]});Q27=makeQuery(id+"F0.imprint","IMPRINT",FACE,{"disambiguationData":[TD([[makeQuery(id+"F0.imprint","IMPRINT",EDGE,{"disambiguationData":[TD([[subQ2,-1.0]])],"derivedFrom":subQ1}),1.0]])]});}
            var Q28;
            {var subQ0=sQuery(id+"F0.wireOp",EDGE,"E20.0");var subQ1=sQuery(id+"F0.wireOp",EDGE,"E0");var subQ2=makeQuery(id+"F0.imprint","INTERSECT",VERTEX,{"derivedFrom":[subQ1,subQ0]});Q28=makeQuery(id+"F0.imprint","IMPRINT",FACE,{"disambiguationData":[TD([[makeQuery(id+"F0.imprint","IMPRINT",EDGE,{"disambiguationData":[TD([[subQ2,-1.0]])],"derivedFrom":subQ1}),-1.0]])]});}
            var Q29;
            {var subQ0=sQuery(id+"F0.wireOp",EDGE,"E75.1.13");Q29=makeQuery(id+"F0.imprint","IMPRINT",FACE,{"disambiguationData":[TD([[makeQuery(id+"F0.imprint","IMPRINT",EDGE,{"derivedFrom":subQ0}),-1.0]])]});}
            var Q30;
            {var subQ0=sQuery(id+"F0.wireOp",EDGE,"E75.1.12");var subQ1=sQuery(id+"F0.wireOp",EDGE,"E0");var subQ2=makeQuery(id+"F0.imprint","INTERSECT",VERTEX,{"derivedFrom":[subQ1,subQ0]});Q30=makeQuery(id+"F0.imprint","IMPRINT",FACE,{"disambiguationData":[TD([[makeQuery(id+"F0.imprint","IMPRINT",EDGE,{"disambiguationData":[TD([[subQ2,-1.0]])],"derivedFrom":subQ1}),1.0]])]});}
            var Q31;
            {var subQ0=sQuery(id+"F0.wireOp",EDGE,"E75.1.12");var subQ1=sQuery(id+"F0.wireOp",EDGE,"E0");var subQ2=makeQuery(id+"F0.imprint","INTERSECT",VERTEX,{"derivedFrom":[subQ1,subQ0]});Q31=makeQuery(id+"F0.imprint","IMPRINT",FACE,{"disambiguationData":[TD([[makeQuery(id+"F0.imprint","IMPRINT",EDGE,{"disambiguationData":[TD([[subQ2,-1.0]])],"derivedFrom":subQ1}),-1.0]])]});}
            var Q32;
            {var subQ0=sQuery(id+"F0.wireOp",EDGE,"E75.1.10");Q32=makeQuery(id+"F0.imprint","IMPRINT",FACE,{"disambiguationData":[TD([[makeQuery(id+"F0.imprint","IMPRINT",EDGE,{"derivedFrom":subQ0}),1.0]])]});}
            var Q33;
            {var subQ0=sQuery(id+"F0.wireOp",EDGE,"E21.0");var subQ1=sQuery(id+"F0.wireOp",EDGE,"E0");var subQ2=makeQuery(id+"F0.imprint","INTERSECT",VERTEX,{"derivedFrom":[subQ1,subQ0]});Q33=makeQuery(id+"F0.imprint","IMPRINT",FACE,{"disambiguationData":[TD([[makeQuery(id+"F0.imprint","IMPRINT",EDGE,{"disambiguationData":[TD([[subQ2,-1.0]])],"derivedFrom":subQ1}),1.0]])]});}
            var Q34;
            {var subQ0=sQuery(id+"F0.wireOp",EDGE,"E21.0");var subQ1=sQuery(id+"F0.wireOp",EDGE,"E0");var subQ2=makeQuery(id+"F0.imprint","INTERSECT",VERTEX,{"derivedFrom":[subQ1,subQ0]});Q34=makeQuery(id+"F0.imprint","IMPRINT",FACE,{"disambiguationData":[TD([[makeQuery(id+"F0.imprint","IMPRINT",EDGE,{"disambiguationData":[TD([[subQ2,-1.0]])],"derivedFrom":subQ1}),-1.0]])]});}
            var Q35;
            {var subQ0=sQuery(id+"F0.wireOp",EDGE,"E75.1.11");Q35=makeQuery(id+"F0.imprint","IMPRINT",FACE,{"disambiguationData":[TD([[makeQuery(id+"F0.imprint","IMPRINT",EDGE,{"derivedFrom":subQ0}),-1.0]])]});}
            var Q36;
            {var subQ0=sQuery(id+"F0.wireOp",EDGE,"E75.1.9");var subQ1=sQuery(id+"F0.wireOp",EDGE,"E0");var subQ2=makeQuery(id+"F0.imprint","INTERSECT",VERTEX,{"derivedFrom":[subQ1,subQ0]});Q36=makeQuery(id+"F0.imprint","IMPRINT",FACE,{"disambiguationData":[TD([[makeQuery(id+"F0.imprint","IMPRINT",EDGE,{"disambiguationData":[TD([[subQ2,-1.0]])],"derivedFrom":subQ1}),-1.0]])]});}
            var Q37;
            {var subQ0=sQuery(id+"F0.wireOp",EDGE,"E75.1.9");var subQ1=sQuery(id+"F0.wireOp",EDGE,"E0");var subQ2=makeQuery(id+"F0.imprint","INTERSECT",VERTEX,{"derivedFrom":[subQ1,subQ0]});Q37=makeQuery(id+"F0.imprint","IMPRINT",FACE,{"disambiguationData":[TD([[makeQuery(id+"F0.imprint","IMPRINT",EDGE,{"disambiguationData":[TD([[subQ2,-1.0]])],"derivedFrom":subQ1}),1.0]])]});}
            var Q38;
            {var subQ0=sQuery(id+"F0.wireOp",EDGE,"E75.1.7");Q38=makeQuery(id+"F0.imprint","IMPRINT",FACE,{"disambiguationData":[TD([[makeQuery(id+"F0.imprint","IMPRINT",EDGE,{"derivedFrom":subQ0}),1.0]])]});}
            var Q39;
            {var subQ0=sQuery(id+"F0.wireOp",EDGE,"E22.0");var subQ1=sQuery(id+"F0.wireOp",EDGE,"E0");var subQ2=makeQuery(id+"F0.imprint","INTERSECT",VERTEX,{"derivedFrom":[subQ1,subQ0]});Q39=makeQuery(id+"F0.imprint","IMPRINT",FACE,{"disambiguationData":[TD([[makeQuery(id+"F0.imprint","IMPRINT",EDGE,{"disambiguationData":[TD([[subQ2,-1.0]])],"derivedFrom":subQ1}),1.0]])]});}
            var Q40;
            {var subQ0=sQuery(id+"F0.wireOp",EDGE,"E22.0");var subQ1=sQuery(id+"F0.wireOp",EDGE,"E0");var subQ2=makeQuery(id+"F0.imprint","INTERSECT",VERTEX,{"derivedFrom":[subQ1,subQ0]});Q40=makeQuery(id+"F0.imprint","IMPRINT",FACE,{"disambiguationData":[TD([[makeQuery(id+"F0.imprint","IMPRINT",EDGE,{"disambiguationData":[TD([[subQ2,-1.0]])],"derivedFrom":subQ1}),-1.0]])]});}
            var Q41;
            {var subQ0=sQuery(id+"F0.wireOp",EDGE,"E75.1.8");Q41=makeQuery(id+"F0.imprint","IMPRINT",FACE,{"disambiguationData":[TD([[makeQuery(id+"F0.imprint","IMPRINT",EDGE,{"derivedFrom":subQ0}),-1.0]])]});}
            var Q42;
            {var subQ0=sQuery(id+"F0.wireOp",EDGE,"E75.1.6");var subQ1=sQuery(id+"F0.wireOp",EDGE,"E0");var subQ2=makeQuery(id+"F0.imprint","INTERSECT",VERTEX,{"derivedFrom":[subQ1,subQ0]});Q42=makeQuery(id+"F0.imprint","IMPRINT",FACE,{"disambiguationData":[TD([[makeQuery(id+"F0.imprint","IMPRINT",EDGE,{"disambiguationData":[TD([[subQ2,-1.0]])],"derivedFrom":subQ1}),-1.0]])]});}
            var Q43;
            {var subQ0=sQuery(id+"F0.wireOp",EDGE,"E75.1.6");var subQ1=sQuery(id+"F0.wireOp",EDGE,"E0");var subQ2=makeQuery(id+"F0.imprint","INTERSECT",VERTEX,{"derivedFrom":[subQ1,subQ0]});Q43=makeQuery(id+"F0.imprint","IMPRINT",FACE,{"disambiguationData":[TD([[makeQuery(id+"F0.imprint","IMPRINT",EDGE,{"disambiguationData":[TD([[subQ2,-1.0]])],"derivedFrom":subQ1}),1.0]])]});}
            var Q44;
            {var subQ0=sQuery(id+"F0.wireOp",EDGE,"E75.1.5");Q44=makeQuery(id+"F0.imprint","IMPRINT",FACE,{"disambiguationData":[TD([[makeQuery(id+"F0.imprint","IMPRINT",EDGE,{"derivedFrom":subQ0}),1.0]])]});}
            var Q45;
            {var subQ0=sQuery(id+"F0.wireOp",EDGE,"E23.0");var subQ1=sQuery(id+"F0.wireOp",EDGE,"E0");var subQ2=makeQuery(id+"F0.imprint","INTERSECT",VERTEX,{"derivedFrom":[subQ1,subQ0]});Q45=makeQuery(id+"F0.imprint","IMPRINT",FACE,{"disambiguationData":[TD([[makeQuery(id+"F0.imprint","IMPRINT",EDGE,{"disambiguationData":[TD([[subQ2,-1.0]])],"derivedFrom":subQ1}),1.0]])]});}
            var Q46;
            {var subQ0=sQuery(id+"F0.wireOp",EDGE,"E23.0");var subQ1=sQuery(id+"F0.wireOp",EDGE,"E0");var subQ2=makeQuery(id+"F0.imprint","INTERSECT",VERTEX,{"derivedFrom":[subQ1,subQ0]});Q46=makeQuery(id+"F0.imprint","IMPRINT",FACE,{"disambiguationData":[TD([[makeQuery(id+"F0.imprint","IMPRINT",EDGE,{"disambiguationData":[TD([[subQ2,-1.0]])],"derivedFrom":subQ1}),-1.0]])]});}
            var Q47;
            {var subQ0=sQuery(id+"F0.wireOp",EDGE,"E24.0");var subQ1=sQuery(id+"F0.wireOp",EDGE,"E0");var subQ2=makeQuery(id+"F0.imprint","INTERSECT",VERTEX,{"derivedFrom":[subQ1,subQ0]});Q47=makeQuery(id+"F0.imprint","IMPRINT",FACE,{"disambiguationData":[TD([[makeQuery(id+"F0.imprint","IMPRINT",EDGE,{"disambiguationData":[TD([[subQ2,1.0]])],"derivedFrom":subQ1}),1.0]])]});}
            var Q48;
            {var subQ0=sQuery(id+"F0.wireOp",EDGE,"E75.1.4");Q48=makeQuery(id+"F0.imprint","IMPRINT",FACE,{"disambiguationData":[TD([[makeQuery(id+"F0.imprint","IMPRINT",EDGE,{"derivedFrom":subQ0}),-1.0]])]});}
            var Q49;
            {var subQ0=sQuery(id+"F0.wireOp",EDGE,"E24.0");var subQ1=sQuery(id+"F0.wireOp",EDGE,"E0");var subQ2=makeQuery(id+"F0.imprint","INTERSECT",VERTEX,{"derivedFrom":[subQ1,subQ0]});Q49=makeQuery(id+"F0.imprint","IMPRINT",FACE,{"disambiguationData":[TD([[makeQuery(id+"F0.imprint","IMPRINT",EDGE,{"disambiguationData":[TD([[subQ2,1.0]])],"derivedFrom":subQ1}),-1.0]])]});}
            var Q50;
            Q50=makeQuery(id+"F0.imprint","IMPRINT",FACE,{"disambiguationData":[TD([[makeQuery(id+"F0.imprint","IMPRINT",EDGE,{"derivedFrom":sQuery(id+"F0.wireOp",EDGE,"E75.1.0")}),-1.0]])]});
            extrude(context, id + "F3", {"entities" : qUnion([Q0, Q1, Q2, Q3, Q4, Q5, Q6, Q7, Q8, Q9, Q10, Q11, Q12, Q13, Q14, Q15, Q16, Q17, Q18, Q19, Q20, Q21, Q22, Q23, Q24, Q25, Q26, Q27, Q28, Q29, Q30, Q31, Q32, Q33, Q34, Q35, Q36, Q37, Q38, Q39, Q40, Q41, Q42, Q43, Q44, Q45, Q46, Q47, Q48, Q49, Q50]), "operationType" : NewBodyOperationType.ADD, "depth" : 12.7 * mm});
        }
        {
            var Q0;
            {var subQ0=sQuery(id+"F0.wireOp",EDGE,"E30");Q0=makeQuery(id+"F0.imprint","IMPRINT",FACE,{"disambiguationData":[TD([[makeQuery(id+"F0.imprint","IMPRINT",EDGE,{"derivedFrom":subQ0}),-1.0]])]});}
            var Q1;
            {var subQ0=sQuery(id+"F0.wireOp",EDGE,"E30");Q1=makeQuery(id+"F0.imprint","IMPRINT",FACE,{"disambiguationData":[TD([[makeQuery(id+"F0.imprint","IMPRINT",EDGE,{"derivedFrom":subQ0}),1.0]])]});}
            var Q2;
            {var subQ1=sQuery(id+"F0.wireOp",EDGE,"E11");var subQ3=sQuery(id+"F0.wireOp",EDGE,"E75.3.25");var subQ4=makeQuery(id+"F0.imprint","INTERSECT",VERTEX,{"derivedFrom":[subQ1,subQ3]});Q2=makeQuery(id+"F0.imprint","IMPRINT",FACE,{"disambiguationData":[TD([[makeQuery(id+"F0.imprint","IMPRINT",EDGE,{"disambiguationData":[TD([[subQ4,-1.0]])],"derivedFrom":subQ3}),-1.0]])]});}
            var Q3;
            {var subQ1=sQuery(id+"F0.wireOp",EDGE,"E11");var subQ3=sQuery(id+"F0.wireOp",EDGE,"E75.3.25");var subQ4=makeQuery(id+"F0.imprint","INTERSECT",VERTEX,{"derivedFrom":[subQ1,subQ3]});Q3=makeQuery(id+"F0.imprint","IMPRINT",FACE,{"disambiguationData":[TD([[makeQuery(id+"F0.imprint","IMPRINT",EDGE,{"disambiguationData":[TD([[subQ4,1.0]])],"derivedFrom":subQ3}),-1.0]])]});}
            var Q4;
            {var subQ0=sQuery(id+"F0.wireOp",EDGE,"E75.3.26");Q4=makeQuery(id+"F0.imprint","IMPRINT",FACE,{"disambiguationData":[TD([[makeQuery(id+"F0.imprint","IMPRINT",EDGE,{"derivedFrom":subQ0}),-1.0]])]});}
            var Q5;
            {var subQ0=sQuery(id+"F0.wireOp",EDGE,"E75.3.24");Q5=makeQuery(id+"F0.imprint","IMPRINT",FACE,{"disambiguationData":[TD([[makeQuery(id+"F0.imprint","IMPRINT",EDGE,{"derivedFrom":subQ0}),1.0]])]});}
            var Q6;
            {var subQ0=sQuery(id+"F0.wireOp",EDGE,"E25.2.7");var subQ1=sQuery(id+"F0.wireOp",EDGE,"E11");var subQ2=makeQuery(id+"F0.imprint","INTERSECT",VERTEX,{"derivedFrom":[subQ1,subQ0]});Q6=makeQuery(id+"F0.imprint","IMPRINT",FACE,{"disambiguationData":[TD([[makeQuery(id+"F0.imprint","IMPRINT",EDGE,{"disambiguationData":[TD([[subQ2,-1.0]])],"derivedFrom":subQ1}),1.0]])]});}
            var Q7;
            {var subQ0=sQuery(id+"F0.wireOp",EDGE,"E25.2.7");var subQ1=sQuery(id+"F0.wireOp",EDGE,"E11");var subQ2=makeQuery(id+"F0.imprint","INTERSECT",VERTEX,{"derivedFrom":[subQ1,subQ0]});Q7=makeQuery(id+"F0.imprint","IMPRINT",FACE,{"disambiguationData":[TD([[makeQuery(id+"F0.imprint","IMPRINT",EDGE,{"disambiguationData":[TD([[subQ2,-1.0]])],"derivedFrom":subQ1}),-1.0]])]});}
            var Q8;
            {var subQ0=sQuery(id+"F0.wireOp",EDGE,"E75.3.23");Q8=makeQuery(id+"F0.imprint","IMPRINT",FACE,{"disambiguationData":[TD([[makeQuery(id+"F0.imprint","IMPRINT",EDGE,{"derivedFrom":subQ0}),-1.0]])]});}
            var Q9;
            {var subQ0=sQuery(id+"F0.wireOp",EDGE,"E75.3.21");var subQ1=sQuery(id+"F0.wireOp",EDGE,"E11");var subQ2=makeQuery(id+"F0.imprint","INTERSECT",VERTEX,{"derivedFrom":[subQ1,subQ0]});Q9=makeQuery(id+"F0.imprint","IMPRINT",FACE,{"disambiguationData":[TD([[makeQuery(id+"F0.imprint","IMPRINT",EDGE,{"disambiguationData":[TD([[subQ2,-1.0]])],"derivedFrom":subQ1}),-1.0]])]});}
            var Q10;
            {var subQ0=sQuery(id+"F0.wireOp",EDGE,"E75.3.21");var subQ1=sQuery(id+"F0.wireOp",EDGE,"E11");var subQ2=makeQuery(id+"F0.imprint","INTERSECT",VERTEX,{"derivedFrom":[subQ1,subQ0]});Q10=makeQuery(id+"F0.imprint","IMPRINT",FACE,{"disambiguationData":[TD([[makeQuery(id+"F0.imprint","IMPRINT",EDGE,{"disambiguationData":[TD([[subQ2,-1.0]])],"derivedFrom":subQ1}),1.0]])]});}
            var Q11;
            {var subQ0=sQuery(id+"F0.wireOp",EDGE,"E75.3.22");Q11=makeQuery(id+"F0.imprint","IMPRINT",FACE,{"disambiguationData":[TD([[makeQuery(id+"F0.imprint","IMPRINT",EDGE,{"derivedFrom":subQ0}),1.0]])]});}
            var Q12;
            {var subQ0=sQuery(id+"F0.wireOp",EDGE,"E75.3.20");Q12=makeQuery(id+"F0.imprint","IMPRINT",FACE,{"disambiguationData":[TD([[makeQuery(id+"F0.imprint","IMPRINT",EDGE,{"derivedFrom":subQ0}),-1.0]])]});}
            var Q13;
            {var subQ0=sQuery(id+"F0.wireOp",EDGE,"E75.3.18");var subQ1=sQuery(id+"F0.wireOp",EDGE,"E11");var subQ2=makeQuery(id+"F0.imprint","INTERSECT",VERTEX,{"derivedFrom":[subQ1,subQ0]});Q13=makeQuery(id+"F0.imprint","IMPRINT",FACE,{"disambiguationData":[TD([[makeQuery(id+"F0.imprint","IMPRINT",EDGE,{"disambiguationData":[TD([[subQ2,-1.0]])],"derivedFrom":subQ1}),-1.0]])]});}
            var Q14;
            {var subQ0=sQuery(id+"F0.wireOp",EDGE,"E75.3.18");var subQ1=sQuery(id+"F0.wireOp",EDGE,"E11");var subQ2=makeQuery(id+"F0.imprint","INTERSECT",VERTEX,{"derivedFrom":[subQ1,subQ0]});Q14=makeQuery(id+"F0.imprint","IMPRINT",FACE,{"disambiguationData":[TD([[makeQuery(id+"F0.imprint","IMPRINT",EDGE,{"disambiguationData":[TD([[subQ2,-1.0]])],"derivedFrom":subQ1}),1.0]])]});}
            var Q15;
            {var subQ0=sQuery(id+"F0.wireOp",EDGE,"E75.3.19");Q15=makeQuery(id+"F0.imprint","IMPRINT",FACE,{"disambiguationData":[TD([[makeQuery(id+"F0.imprint","IMPRINT",EDGE,{"derivedFrom":subQ0}),1.0]])]});}
            var Q16;
            {var subQ0=sQuery(id+"F0.wireOp",EDGE,"E25.2.6");var subQ1=sQuery(id+"F0.wireOp",EDGE,"E11");var subQ2=makeQuery(id+"F0.imprint","INTERSECT",VERTEX,{"derivedFrom":[subQ1,subQ0]});Q16=makeQuery(id+"F0.imprint","IMPRINT",FACE,{"disambiguationData":[TD([[makeQuery(id+"F0.imprint","IMPRINT",EDGE,{"disambiguationData":[TD([[subQ2,-1.0]])],"derivedFrom":subQ1}),1.0]])]});}
            var Q17;
            {var subQ0=sQuery(id+"F0.wireOp",EDGE,"E25.2.6");var subQ1=sQuery(id+"F0.wireOp",EDGE,"E11");var subQ2=makeQuery(id+"F0.imprint","INTERSECT",VERTEX,{"derivedFrom":[subQ1,subQ0]});Q17=makeQuery(id+"F0.imprint","IMPRINT",FACE,{"disambiguationData":[TD([[makeQuery(id+"F0.imprint","IMPRINT",EDGE,{"disambiguationData":[TD([[subQ2,-1.0]])],"derivedFrom":subQ1}),-1.0]])]});}
            var Q18;
            {var subQ0=sQuery(id+"F0.wireOp",EDGE,"E25.2.5");var subQ1=sQuery(id+"F0.wireOp",EDGE,"E11");var subQ2=makeQuery(id+"F0.imprint","INTERSECT",VERTEX,{"derivedFrom":[subQ1,subQ0]});Q18=makeQuery(id+"F0.imprint","IMPRINT",FACE,{"disambiguationData":[TD([[makeQuery(id+"F0.imprint","IMPRINT",EDGE,{"disambiguationData":[TD([[subQ2,-1.0]])],"derivedFrom":subQ1}),-1.0]])]});}
            var Q19;
            {var subQ0=sQuery(id+"F0.wireOp",EDGE,"E25.2.5");var subQ1=sQuery(id+"F0.wireOp",EDGE,"E11");var subQ2=makeQuery(id+"F0.imprint","INTERSECT",VERTEX,{"derivedFrom":[subQ1,subQ0]});Q19=makeQuery(id+"F0.imprint","IMPRINT",FACE,{"disambiguationData":[TD([[makeQuery(id+"F0.imprint","IMPRINT",EDGE,{"disambiguationData":[TD([[subQ2,-1.0]])],"derivedFrom":subQ1}),1.0]])]});}
            var Q20;
            {var subQ0=sQuery(id+"F0.wireOp",EDGE,"E75.3.15");var subQ1=sQuery(id+"F0.wireOp",EDGE,"E11");var subQ2=makeQuery(id+"F0.imprint","INTERSECT",VERTEX,{"derivedFrom":[subQ1,subQ0]});Q20=makeQuery(id+"F0.imprint","IMPRINT",FACE,{"disambiguationData":[TD([[makeQuery(id+"F0.imprint","IMPRINT",EDGE,{"disambiguationData":[TD([[subQ2,-1.0]])],"derivedFrom":subQ1}),1.0]])]});}
            var Q21;
            {var subQ0=sQuery(id+"F0.wireOp",EDGE,"E75.3.15");var subQ1=sQuery(id+"F0.wireOp",EDGE,"E11");var subQ2=makeQuery(id+"F0.imprint","INTERSECT",VERTEX,{"derivedFrom":[subQ1,subQ0]});Q21=makeQuery(id+"F0.imprint","IMPRINT",FACE,{"disambiguationData":[TD([[makeQuery(id+"F0.imprint","IMPRINT",EDGE,{"disambiguationData":[TD([[subQ2,-1.0]])],"derivedFrom":subQ1}),-1.0]])]});}
            var Q22;
            {var subQ0=sQuery(id+"F0.wireOp",EDGE,"E75.3.16");Q22=makeQuery(id+"F0.imprint","IMPRINT",FACE,{"disambiguationData":[TD([[makeQuery(id+"F0.imprint","IMPRINT",EDGE,{"derivedFrom":subQ0}),1.0]])]});}
            var Q23;
            {var subQ0=sQuery(id+"F0.wireOp",EDGE,"E75.3.17");Q23=makeQuery(id+"F0.imprint","IMPRINT",FACE,{"disambiguationData":[TD([[makeQuery(id+"F0.imprint","IMPRINT",EDGE,{"derivedFrom":subQ0}),-1.0]])]});}
            var Q24;
            {var subQ0=sQuery(id+"F0.wireOp",EDGE,"E25.2.4");var subQ1=sQuery(id+"F0.wireOp",EDGE,"E11");var subQ2=makeQuery(id+"F0.imprint","INTERSECT",VERTEX,{"derivedFrom":[subQ1,subQ0]});Q24=makeQuery(id+"F0.imprint","IMPRINT",FACE,{"disambiguationData":[TD([[makeQuery(id+"F0.imprint","IMPRINT",EDGE,{"disambiguationData":[TD([[subQ2,-1.0]])],"derivedFrom":subQ1}),1.0]])]});}
            var Q25;
            {var subQ0=sQuery(id+"F0.wireOp",EDGE,"E25.2.4");var subQ1=sQuery(id+"F0.wireOp",EDGE,"E11");var subQ2=makeQuery(id+"F0.imprint","INTERSECT",VERTEX,{"derivedFrom":[subQ1,subQ0]});Q25=makeQuery(id+"F0.imprint","IMPRINT",FACE,{"disambiguationData":[TD([[makeQuery(id+"F0.imprint","IMPRINT",EDGE,{"disambiguationData":[TD([[subQ2,-1.0]])],"derivedFrom":subQ1}),-1.0]])]});}
            var Q26;
            {var subQ0=sQuery(id+"F0.wireOp",EDGE,"E75.3.12");var subQ1=sQuery(id+"F0.wireOp",EDGE,"E11");var subQ2=makeQuery(id+"F0.imprint","INTERSECT",VERTEX,{"derivedFrom":[subQ1,subQ0]});Q26=makeQuery(id+"F0.imprint","IMPRINT",FACE,{"disambiguationData":[TD([[makeQuery(id+"F0.imprint","IMPRINT",EDGE,{"disambiguationData":[TD([[subQ2,-1.0]])],"derivedFrom":subQ1}),-1.0]])]});}
            var Q27;
            {var subQ0=sQuery(id+"F0.wireOp",EDGE,"E75.3.12");var subQ1=sQuery(id+"F0.wireOp",EDGE,"E11");var subQ2=makeQuery(id+"F0.imprint","INTERSECT",VERTEX,{"derivedFrom":[subQ1,subQ0]});Q27=makeQuery(id+"F0.imprint","IMPRINT",FACE,{"disambiguationData":[TD([[makeQuery(id+"F0.imprint","IMPRINT",EDGE,{"disambiguationData":[TD([[subQ2,-1.0]])],"derivedFrom":subQ1}),1.0]])]});}
            var Q28;
            {var subQ0=sQuery(id+"F0.wireOp",EDGE,"E75.3.13");Q28=makeQuery(id+"F0.imprint","IMPRINT",FACE,{"disambiguationData":[TD([[makeQuery(id+"F0.imprint","IMPRINT",EDGE,{"derivedFrom":subQ0}),-1.0]])]});}
            var Q29;
            {var subQ0=sQuery(id+"F0.wireOp",EDGE,"E25.2.3");var subQ1=sQuery(id+"F0.wireOp",EDGE,"E11");var subQ2=makeQuery(id+"F0.imprint","INTERSECT",VERTEX,{"derivedFrom":[subQ1,subQ0]});Q29=makeQuery(id+"F0.imprint","IMPRINT",FACE,{"disambiguationData":[TD([[makeQuery(id+"F0.imprint","IMPRINT",EDGE,{"disambiguationData":[TD([[subQ2,-1.0]])],"derivedFrom":subQ1}),1.0]])]});}
            var Q30;
            {var subQ0=sQuery(id+"F0.wireOp",EDGE,"E75.3.14");Q30=makeQuery(id+"F0.imprint","IMPRINT",FACE,{"disambiguationData":[TD([[makeQuery(id+"F0.imprint","IMPRINT",EDGE,{"derivedFrom":subQ0}),1.0]])]});}
            var Q31;
            {var subQ0=sQuery(id+"F0.wireOp",EDGE,"E25.2.3");var subQ1=sQuery(id+"F0.wireOp",EDGE,"E11");var subQ2=makeQuery(id+"F0.imprint","INTERSECT",VERTEX,{"derivedFrom":[subQ1,subQ0]});Q31=makeQuery(id+"F0.imprint","IMPRINT",FACE,{"disambiguationData":[TD([[makeQuery(id+"F0.imprint","IMPRINT",EDGE,{"disambiguationData":[TD([[subQ2,-1.0]])],"derivedFrom":subQ1}),-1.0]])]});}
            var Q32;
            {var subQ0=sQuery(id+"F0.wireOp",EDGE,"E75.3.9");var subQ1=sQuery(id+"F0.wireOp",EDGE,"E11");var subQ2=makeQuery(id+"F0.imprint","INTERSECT",VERTEX,{"derivedFrom":[subQ1,subQ0]});Q32=makeQuery(id+"F0.imprint","IMPRINT",FACE,{"disambiguationData":[TD([[makeQuery(id+"F0.imprint","IMPRINT",EDGE,{"disambiguationData":[TD([[subQ2,-1.0]])],"derivedFrom":subQ1}),-1.0]])]});}
            var Q33;
            {var subQ0=sQuery(id+"F0.wireOp",EDGE,"E75.3.10");Q33=makeQuery(id+"F0.imprint","IMPRINT",FACE,{"disambiguationData":[TD([[makeQuery(id+"F0.imprint","IMPRINT",EDGE,{"derivedFrom":subQ0}),1.0]])]});}
            var Q34;
            {var subQ0=sQuery(id+"F0.wireOp",EDGE,"E75.3.9");var subQ1=sQuery(id+"F0.wireOp",EDGE,"E11");var subQ2=makeQuery(id+"F0.imprint","INTERSECT",VERTEX,{"derivedFrom":[subQ1,subQ0]});Q34=makeQuery(id+"F0.imprint","IMPRINT",FACE,{"disambiguationData":[TD([[makeQuery(id+"F0.imprint","IMPRINT",EDGE,{"disambiguationData":[TD([[subQ2,-1.0]])],"derivedFrom":subQ1}),1.0]])]});}
            var Q35;
            {var subQ0=sQuery(id+"F0.wireOp",EDGE,"E75.3.11");Q35=makeQuery(id+"F0.imprint","IMPRINT",FACE,{"disambiguationData":[TD([[makeQuery(id+"F0.imprint","IMPRINT",EDGE,{"derivedFrom":subQ0}),-1.0]])]});}
            var Q36;
            {var subQ0=sQuery(id+"F0.wireOp",EDGE,"E25.2.2");var subQ1=sQuery(id+"F0.wireOp",EDGE,"E11");var subQ2=makeQuery(id+"F0.imprint","INTERSECT",VERTEX,{"derivedFrom":[subQ1,subQ0]});Q36=makeQuery(id+"F0.imprint","IMPRINT",FACE,{"disambiguationData":[TD([[makeQuery(id+"F0.imprint","IMPRINT",EDGE,{"disambiguationData":[TD([[subQ2,-1.0]])],"derivedFrom":subQ1}),1.0]])]});}
            var Q37;
            {var subQ0=sQuery(id+"F0.wireOp",EDGE,"E25.2.2");var subQ1=sQuery(id+"F0.wireOp",EDGE,"E11");var subQ2=makeQuery(id+"F0.imprint","INTERSECT",VERTEX,{"derivedFrom":[subQ1,subQ0]});Q37=makeQuery(id+"F0.imprint","IMPRINT",FACE,{"disambiguationData":[TD([[makeQuery(id+"F0.imprint","IMPRINT",EDGE,{"disambiguationData":[TD([[subQ2,-1.0]])],"derivedFrom":subQ1}),-1.0]])]});}
            var Q38;
            {var subQ0=sQuery(id+"F0.wireOp",EDGE,"E75.3.6");var subQ1=sQuery(id+"F0.wireOp",EDGE,"E11");var subQ2=makeQuery(id+"F0.imprint","INTERSECT",VERTEX,{"derivedFrom":[subQ1,subQ0]});Q38=makeQuery(id+"F0.imprint","IMPRINT",FACE,{"disambiguationData":[TD([[makeQuery(id+"F0.imprint","IMPRINT",EDGE,{"disambiguationData":[TD([[subQ2,-1.0]])],"derivedFrom":subQ1}),-1.0]])]});}
            var Q39;
            {var subQ0=sQuery(id+"F0.wireOp",EDGE,"E75.3.7");Q39=makeQuery(id+"F0.imprint","IMPRINT",FACE,{"disambiguationData":[TD([[makeQuery(id+"F0.imprint","IMPRINT",EDGE,{"derivedFrom":subQ0}),1.0]])]});}
            var Q40;
            {var subQ0=sQuery(id+"F0.wireOp",EDGE,"E75.3.6");var subQ1=sQuery(id+"F0.wireOp",EDGE,"E11");var subQ2=makeQuery(id+"F0.imprint","INTERSECT",VERTEX,{"derivedFrom":[subQ1,subQ0]});Q40=makeQuery(id+"F0.imprint","IMPRINT",FACE,{"disambiguationData":[TD([[makeQuery(id+"F0.imprint","IMPRINT",EDGE,{"disambiguationData":[TD([[subQ2,-1.0]])],"derivedFrom":subQ1}),1.0]])]});}
            var Q41;
            {var subQ0=sQuery(id+"F0.wireOp",EDGE,"E75.3.8");Q41=makeQuery(id+"F0.imprint","IMPRINT",FACE,{"disambiguationData":[TD([[makeQuery(id+"F0.imprint","IMPRINT",EDGE,{"derivedFrom":subQ0}),-1.0]])]});}
            var Q42;
            {var subQ0=sQuery(id+"F0.wireOp",EDGE,"E25.2.1");var subQ1=sQuery(id+"F0.wireOp",EDGE,"E11");var subQ2=makeQuery(id+"F0.imprint","INTERSECT",VERTEX,{"derivedFrom":[subQ1,subQ0]});Q42=makeQuery(id+"F0.imprint","IMPRINT",FACE,{"disambiguationData":[TD([[makeQuery(id+"F0.imprint","IMPRINT",EDGE,{"disambiguationData":[TD([[subQ2,-1.0]])],"derivedFrom":subQ1}),1.0]])]});}
            var Q43;
            {var subQ0=sQuery(id+"F0.wireOp",EDGE,"E25.2.1");var subQ1=sQuery(id+"F0.wireOp",EDGE,"E11");var subQ2=makeQuery(id+"F0.imprint","INTERSECT",VERTEX,{"derivedFrom":[subQ1,subQ0]});Q43=makeQuery(id+"F0.imprint","IMPRINT",FACE,{"disambiguationData":[TD([[makeQuery(id+"F0.imprint","IMPRINT",EDGE,{"disambiguationData":[TD([[subQ2,-1.0]])],"derivedFrom":subQ1}),-1.0]])]});}
            var Q44;
            {var subQ0=sQuery(id+"F0.wireOp",EDGE,"E75.3.3");var subQ1=sQuery(id+"F0.wireOp",EDGE,"E11");var subQ2=makeQuery(id+"F0.imprint","INTERSECT",VERTEX,{"derivedFrom":[subQ1,subQ0]});Q44=makeQuery(id+"F0.imprint","IMPRINT",FACE,{"disambiguationData":[TD([[makeQuery(id+"F0.imprint","IMPRINT",EDGE,{"disambiguationData":[TD([[subQ2,-1.0]])],"derivedFrom":subQ1}),-1.0]])]});}
            var Q45;
            {var subQ0=sQuery(id+"F0.wireOp",EDGE,"E75.3.5");Q45=makeQuery(id+"F0.imprint","IMPRINT",FACE,{"disambiguationData":[TD([[makeQuery(id+"F0.imprint","IMPRINT",EDGE,{"derivedFrom":subQ0}),1.0]])]});}
            var Q46;
            {var subQ0=sQuery(id+"F0.wireOp",EDGE,"E75.3.3");var subQ1=sQuery(id+"F0.wireOp",EDGE,"E11");var subQ2=makeQuery(id+"F0.imprint","INTERSECT",VERTEX,{"derivedFrom":[subQ1,subQ0]});Q46=makeQuery(id+"F0.imprint","IMPRINT",FACE,{"disambiguationData":[TD([[makeQuery(id+"F0.imprint","IMPRINT",EDGE,{"disambiguationData":[TD([[subQ2,-1.0]])],"derivedFrom":subQ1}),1.0]])]});}
            var Q47;
            {var subQ0=sQuery(id+"F0.wireOp",EDGE,"E75.3.4");Q47=makeQuery(id+"F0.imprint","IMPRINT",FACE,{"disambiguationData":[TD([[makeQuery(id+"F0.imprint","IMPRINT",EDGE,{"derivedFrom":subQ0}),-1.0]])]});}
            var Q48;
            {var subQ0=sQuery(id+"F0.wireOp",EDGE,"E25.2.0");var subQ1=sQuery(id+"F0.wireOp",EDGE,"E11");var subQ2=makeQuery(id+"F0.imprint","INTERSECT",VERTEX,{"derivedFrom":[subQ1,subQ0]});Q48=makeQuery(id+"F0.imprint","IMPRINT",FACE,{"disambiguationData":[TD([[makeQuery(id+"F0.imprint","IMPRINT",EDGE,{"disambiguationData":[TD([[subQ2,-1.0]])],"derivedFrom":subQ1}),1.0]])]});}
            var Q49;
            {var subQ0=sQuery(id+"F0.wireOp",EDGE,"E25.2.0");var subQ1=sQuery(id+"F0.wireOp",EDGE,"E11");var subQ2=makeQuery(id+"F0.imprint","INTERSECT",VERTEX,{"derivedFrom":[subQ1,subQ0]});Q49=makeQuery(id+"F0.imprint","IMPRINT",FACE,{"disambiguationData":[TD([[makeQuery(id+"F0.imprint","IMPRINT",EDGE,{"disambiguationData":[TD([[subQ2,-1.0]])],"derivedFrom":subQ1}),-1.0]])]});}
            var Q50;
            Q50=makeQuery(id+"F0.imprint","IMPRINT",FACE,{"disambiguationData":[TD([[makeQuery(id+"F0.imprint","IMPRINT",EDGE,{"derivedFrom":sQuery(id+"F0.wireOp",EDGE,"E75.3.0")}),-1.0]])]});
            extrude(context, id + "F4", {"entities" : qUnion([Q0, Q1, Q2, Q3, Q4, Q5, Q6, Q7, Q8, Q9, Q10, Q11, Q12, Q13, Q14, Q15, Q16, Q17, Q18, Q19, Q20, Q21, Q22, Q23, Q24, Q25, Q26, Q27, Q28, Q29, Q30, Q31, Q32, Q33, Q34, Q35, Q36, Q37, Q38, Q39, Q40, Q41, Q42, Q43, Q44, Q45, Q46, Q47, Q48, Q49, Q50]), "operationType" : NewBodyOperationType.ADD, "depth" : 12.7 * mm});
        }
        {
            var Q0;
            Q0=makeQuery(id+"F0.imprint","IMPRINT",FACE,{"disambiguationData":[TD([[makeQuery(id+"F0.imprint","IMPRINT",EDGE,{"derivedFrom":sQuery(id+"F0.wireOp",EDGE,"E1")}),1.0]])]});
            extrude(context, id + "F5", {"entities" : qUnion([Q0]), "oppositeDirection" : true, "depth" : 0.53 * mm});
        }
        {
            var Q0;
            Q0=makeQuery(id+"F0.imprint","IMPRINT",FACE,{"disambiguationData":[TD([[makeQuery(id+"F0.imprint","IMPRINT",EDGE,{"derivedFrom":sQuery(id+"F0.wireOp",EDGE,"E1")}),-1.0]])]});
            extrude(context, id + "F6", {"entities" : qUnion([Q0]), "oppositeDirection" : true, "depth" : 0.53 * mm});
        }
        {
            var Q0;
            Q0=makeQuery(id+"F5.opExtrude","CAP_FACE",FACE,{"disambiguationData":[OSD([sQuery(id+"F0.wireOp",EDGE,"E1"),sQuery(id+"F0.wireOp",EDGE,"E2"),sQuery(id+"F0.wireOp",EDGE,"E3"),sQuery(id+"F0.wireOp",EDGE,"E4"),sQuery(id+"F0.wireOp",EDGE,"E5.0"),sQuery(id+"F0.wireOp",EDGE,"E6"),sQuery(id+"F0.wireOp",EDGE,"E8"),sQuery(id+"F0.wireOp",EDGE,"E9.0"),sQuery(id+"F0.wireOp",EDGE,"E10"),sQuery(id+"F0.wireOp",EDGE,"E12"),sQuery(id+"F0.wireOp",EDGE,"E13.0"),sQuery(id+"F0.wireOp",EDGE,"E14"),sQuery(id+"F0.wireOp",EDGE,"E16"),sQuery(id+"F0.wireOp",EDGE,"E17.0"),sQuery(id+"F0.wireOp",EDGE,"E18.0"),sQuery(id+"F0.wireOp",EDGE,"E19.0"),sQuery(id+"F0.wireOp",EDGE,"E20.0"),sQuery(id+"F0.wireOp",EDGE,"E21.0"),sQuery(id+"F0.wireOp",EDGE,"E22.0"),sQuery(id+"F0.wireOp",EDGE,"E23.0"),sQuery(id+"F0.wireOp",EDGE,"E24.0"),sQuery(id+"F0.wireOp",EDGE,"E25.1.0"),sQuery(id+"F0.wireOp",EDGE,"E25.1.1"),sQuery(id+"F0.wireOp",EDGE,"E25.1.2"),sQuery(id+"F0.wireOp",EDGE,"E25.1.3"),sQuery(id+"F0.wireOp",EDGE,"E25.1.4"),sQuery(id+"F0.wireOp",EDGE,"E25.1.5"),sQuery(id+"F0.wireOp",EDGE,"E25.1.6"),sQuery(id+"F0.wireOp",EDGE,"E25.1.7"),sQuery(id+"F0.wireOp",EDGE,"E25.1.8"),sQuery(id+"F0.wireOp",EDGE,"E25.2.0"),sQuery(id+"F0.wireOp",EDGE,"E25.2.1"),sQuery(id+"F0.wireOp",EDGE,"E25.2.2"),sQuery(id+"F0.wireOp",EDGE,"E25.2.3"),sQuery(id+"F0.wireOp",EDGE,"E25.2.4"),sQuery(id+"F0.wireOp",EDGE,"E25.2.5"),sQuery(id+"F0.wireOp",EDGE,"E25.2.6"),sQuery(id+"F0.wireOp",EDGE,"E25.2.7"),sQuery(id+"F0.wireOp",EDGE,"E25.2.8"),sQuery(id+"F0.wireOp",EDGE,"E25.3.0"),sQuery(id+"F0.wireOp",EDGE,"E25.3.1"),sQuery(id+"F0.wireOp",EDGE,"E25.3.2"),sQuery(id+"F0.wireOp",EDGE,"E25.3.3"),sQuery(id+"F0.wireOp",EDGE,"E25.3.4"),sQuery(id+"F0.wireOp",EDGE,"E25.3.5"),sQuery(id+"F0.wireOp",EDGE,"E25.3.6"),sQuery(id+"F0.wireOp",EDGE,"E25.3.7"),sQuery(id+"F0.wireOp",EDGE,"E25.3.8"),sQuery(id+"F0.wireOp",EDGE,"E26"),sQuery(id+"F0.wireOp",EDGE,"E31.0"),sQuery(id+"F0.wireOp",EDGE,"E32.0"),sQuery(id+"F0.wireOp",EDGE,"E33"),sQuery(id+"F0.wireOp",EDGE,"E34"),sQuery(id+"F0.wireOp",EDGE,"E35.0"),sQuery(id+"F0.wireOp",EDGE,"E36.0"),sQuery(id+"F0.wireOp",EDGE,"E37"),sQuery(id+"F0.wireOp",EDGE,"E38"),sQuery(id+"F0.wireOp",EDGE,"E39.0"),sQuery(id+"F0.wireOp",EDGE,"E40.0"),sQuery(id+"F0.wireOp",EDGE,"E41"),sQuery(id+"F0.wireOp",EDGE,"E42"),sQuery(id+"F0.wireOp",EDGE,"E43.0"),sQuery(id+"F0.wireOp",EDGE,"E44.0"),sQuery(id+"F0.wireOp",EDGE,"E45"),sQuery(id+"F0.wireOp",EDGE,"E46"),sQuery(id+"F0.wireOp",EDGE,"E48.0"),sQuery(id+"F0.wireOp",EDGE,"E49"),sQuery(id+"F0.wireOp",EDGE,"E50"),sQuery(id+"F0.wireOp",EDGE,"E51.0"),sQuery(id+"F0.wireOp",EDGE,"E52"),sQuery(id+"F0.wireOp",EDGE,"E53"),sQuery(id+"F0.wireOp",EDGE,"E54.0"),sQuery(id+"F0.wireOp",EDGE,"E55"),sQuery(id+"F0.wireOp",EDGE,"E56"),sQuery(id+"F0.wireOp",EDGE,"E57.0"),sQuery(id+"F0.wireOp",EDGE,"E58"),sQuery(id+"F0.wireOp",EDGE,"E59"),sQuery(id+"F0.wireOp",EDGE,"E60.0"),sQuery(id+"F0.wireOp",EDGE,"E61"),sQuery(id+"F0.wireOp",EDGE,"E62"),sQuery(id+"F0.wireOp",EDGE,"E63.0"),sQuery(id+"F0.wireOp",EDGE,"E64"),sQuery(id+"F0.wireOp",EDGE,"E65"),sQuery(id+"F0.wireOp",EDGE,"E66.0"),sQuery(id+"F0.wireOp",EDGE,"E67"),sQuery(id+"F0.wireOp",EDGE,"E68"),sQuery(id+"F0.wireOp",EDGE,"E69.0"),sQuery(id+"F0.wireOp",EDGE,"E70"),sQuery(id+"F0.wireOp",EDGE,"E71"),sQuery(id+"F0.wireOp",EDGE,"E72.0"),sQuery(id+"F0.wireOp",EDGE,"E73"),sQuery(id+"F0.wireOp",EDGE,"E74"),sQuery(id+"F0.wireOp",EDGE,"E75.1.0"),sQuery(id+"F0.wireOp",EDGE,"E75.1.1"),sQuery(id+"F0.wireOp",EDGE,"E75.1.2"),sQuery(id+"F0.wireOp",EDGE,"E75.1.3"),sQuery(id+"F0.wireOp",EDGE,"E75.1.4"),sQuery(id+"F0.wireOp",EDGE,"E75.1.5"),sQuery(id+"F0.wireOp",EDGE,"E75.1.6"),sQuery(id+"F0.wireOp",EDGE,"E75.1.7"),sQuery(id+"F0.wireOp",EDGE,"E75.1.8"),sQuery(id+"F0.wireOp",EDGE,"E75.1.9"),sQuery(id+"F0.wireOp",EDGE,"E75.1.10"),sQuery(id+"F0.wireOp",EDGE,"E75.1.11"),sQuery(id+"F0.wireOp",EDGE,"E75.1.12"),sQuery(id+"F0.wireOp",EDGE,"E75.1.13"),sQuery(id+"F0.wireOp",EDGE,"E75.1.14"),sQuery(id+"F0.wireOp",EDGE,"E75.1.15"),sQuery(id+"F0.wireOp",EDGE,"E75.1.16"),sQuery(id+"F0.wireOp",EDGE,"E75.1.17"),sQuery(id+"F0.wireOp",EDGE,"E75.1.18"),sQuery(id+"F0.wireOp",EDGE,"E75.1.19"),sQuery(id+"F0.wireOp",EDGE,"E75.1.20"),sQuery(id+"F0.wireOp",EDGE,"E75.1.21"),sQuery(id+"F0.wireOp",EDGE,"E75.1.22"),sQuery(id+"F0.wireOp",EDGE,"E75.1.23"),sQuery(id+"F0.wireOp",EDGE,"E75.1.24"),sQuery(id+"F0.wireOp",EDGE,"E75.1.25"),sQuery(id+"F0.wireOp",EDGE,"E75.1.26"),sQuery(id+"F0.wireOp",EDGE,"E75.2.0"),sQuery(id+"F0.wireOp",EDGE,"E75.2.1"),sQuery(id+"F0.wireOp",EDGE,"E75.2.2"),sQuery(id+"F0.wireOp",EDGE,"E75.2.3"),sQuery(id+"F0.wireOp",EDGE,"E75.2.4"),sQuery(id+"F0.wireOp",EDGE,"E75.2.5"),sQuery(id+"F0.wireOp",EDGE,"E75.2.6"),sQuery(id+"F0.wireOp",EDGE,"E75.2.7"),sQuery(id+"F0.wireOp",EDGE,"E75.2.8"),sQuery(id+"F0.wireOp",EDGE,"E75.2.9"),sQuery(id+"F0.wireOp",EDGE,"E75.2.10"),sQuery(id+"F0.wireOp",EDGE,"E75.2.11"),sQuery(id+"F0.wireOp",EDGE,"E75.2.12"),sQuery(id+"F0.wireOp",EDGE,"E75.2.13"),sQuery(id+"F0.wireOp",EDGE,"E75.2.14"),sQuery(id+"F0.wireOp",EDGE,"E75.2.15"),sQuery(id+"F0.wireOp",EDGE,"E75.2.16"),sQuery(id+"F0.wireOp",EDGE,"E75.2.17"),sQuery(id+"F0.wireOp",EDGE,"E75.2.18"),sQuery(id+"F0.wireOp",EDGE,"E75.2.19"),sQuery(id+"F0.wireOp",EDGE,"E75.2.20"),sQuery(id+"F0.wireOp",EDGE,"E75.2.21"),sQuery(id+"F0.wireOp",EDGE,"E75.2.22"),sQuery(id+"F0.wireOp",EDGE,"E75.2.23"),sQuery(id+"F0.wireOp",EDGE,"E75.2.24"),sQuery(id+"F0.wireOp",EDGE,"E75.2.25"),sQuery(id+"F0.wireOp",EDGE,"E75.2.26"),sQuery(id+"F0.wireOp",EDGE,"E75.3.0"),sQuery(id+"F0.wireOp",EDGE,"E75.3.1"),sQuery(id+"F0.wireOp",EDGE,"E75.3.2"),sQuery(id+"F0.wireOp",EDGE,"E75.3.3"),sQuery(id+"F0.wireOp",EDGE,"E75.3.4"),sQuery(id+"F0.wireOp",EDGE,"E75.3.5"),sQuery(id+"F0.wireOp",EDGE,"E75.3.6"),sQuery(id+"F0.wireOp",EDGE,"E75.3.7"),sQuery(id+"F0.wireOp",EDGE,"E75.3.8"),sQuery(id+"F0.wireOp",EDGE,"E75.3.9"),sQuery(id+"F0.wireOp",EDGE,"E75.3.10"),sQuery(id+"F0.wireOp",EDGE,"E75.3.11"),sQuery(id+"F0.wireOp",EDGE,"E75.3.12"),sQuery(id+"F0.wireOp",EDGE,"E75.3.13"),sQuery(id+"F0.wireOp",EDGE,"E75.3.14"),sQuery(id+"F0.wireOp",EDGE,"E75.3.15"),sQuery(id+"F0.wireOp",EDGE,"E75.3.16"),sQuery(id+"F0.wireOp",EDGE,"E75.3.17"),sQuery(id+"F0.wireOp",EDGE,"E75.3.18"),sQuery(id+"F0.wireOp",EDGE,"E75.3.19"),sQuery(id+"F0.wireOp",EDGE,"E75.3.20"),sQuery(id+"F0.wireOp",EDGE,"E75.3.21"),sQuery(id+"F0.wireOp",EDGE,"E75.3.22"),sQuery(id+"F0.wireOp",EDGE,"E75.3.23"),sQuery(id+"F0.wireOp",EDGE,"E75.3.24"),sQuery(id+"F0.wireOp",EDGE,"E75.3.25"),sQuery(id+"F0.wireOp",EDGE,"E75.3.26")])],"isStart":false});
            var sketch = newSketch(context, id + "F7", { "sketchPlane" : qUnion([Q0])});
            skLineSegment(sketch, "E76.0", {"start": v(-7.62, -1.27) * mm, "end": v(-31.75, -1.27) * mm});
            skArc(sketch, "E76.1", {"start": v(-31.75, -1.27) * mm, "mid": v(-39.37, 6.35) * mm, "end": v(-31.75, 13.97) * mm});
            skLineSegment(sketch, "E76.2", {"start": v(-7.62, 13.97) * mm, "end": v(-31.75, 13.97) * mm});
            skLineSegment(sketch, "E76.3", {"start": v(-7.62, 13.97) * mm, "end": v(-7.62, 38.1) * mm});
            skArc(sketch, "E76.4", {"start": v(-7.62, 38.1) * mm, "mid": v(0, 45.72) * mm, "end": v(7.62, 38.1) * mm});
            skLineSegment(sketch, "E76.5", {"start": v(7.62, 13.97) * mm, "end": v(7.62, 38.1) * mm});
            skLineSegment(sketch, "E76.6", {"start": v(7.62, 13.97) * mm, "end": v(31.75, 13.97) * mm});
            skArc(sketch, "E76.7", {"start": v(31.75, 13.97) * mm, "mid": v(39.37, 6.35) * mm, "end": v(31.75, -1.27) * mm});
            skLineSegment(sketch, "E76.8", {"start": v(7.62, -1.27) * mm, "end": v(31.75, -1.27) * mm});
            skLineSegment(sketch, "E76.9", {"start": v(7.62, -25.4) * mm, "end": v(7.62, -1.27) * mm});
            skArc(sketch, "E76.10", {"start": v(7.62, -25.4) * mm, "mid": v(0, -33.02) * mm, "end": v(-7.62, -25.4) * mm});
            skLineSegment(sketch, "E76.11", {"start": v(-7.62, -25.4) * mm, "end": v(-7.62, -1.27) * mm});
            skSolve(sketch);
        }
        {
            var Q0;
            Q0 = qSketchRegion(id + "F7", true);
            extrude(context, id + "F8", {"entities" : qUnion([Q0]), "operationType" : NewBodyOperationType.ADD, "endBound" : BoundingType.SYMMETRIC, "depth" : 2.54 * mm});
        }
    });
